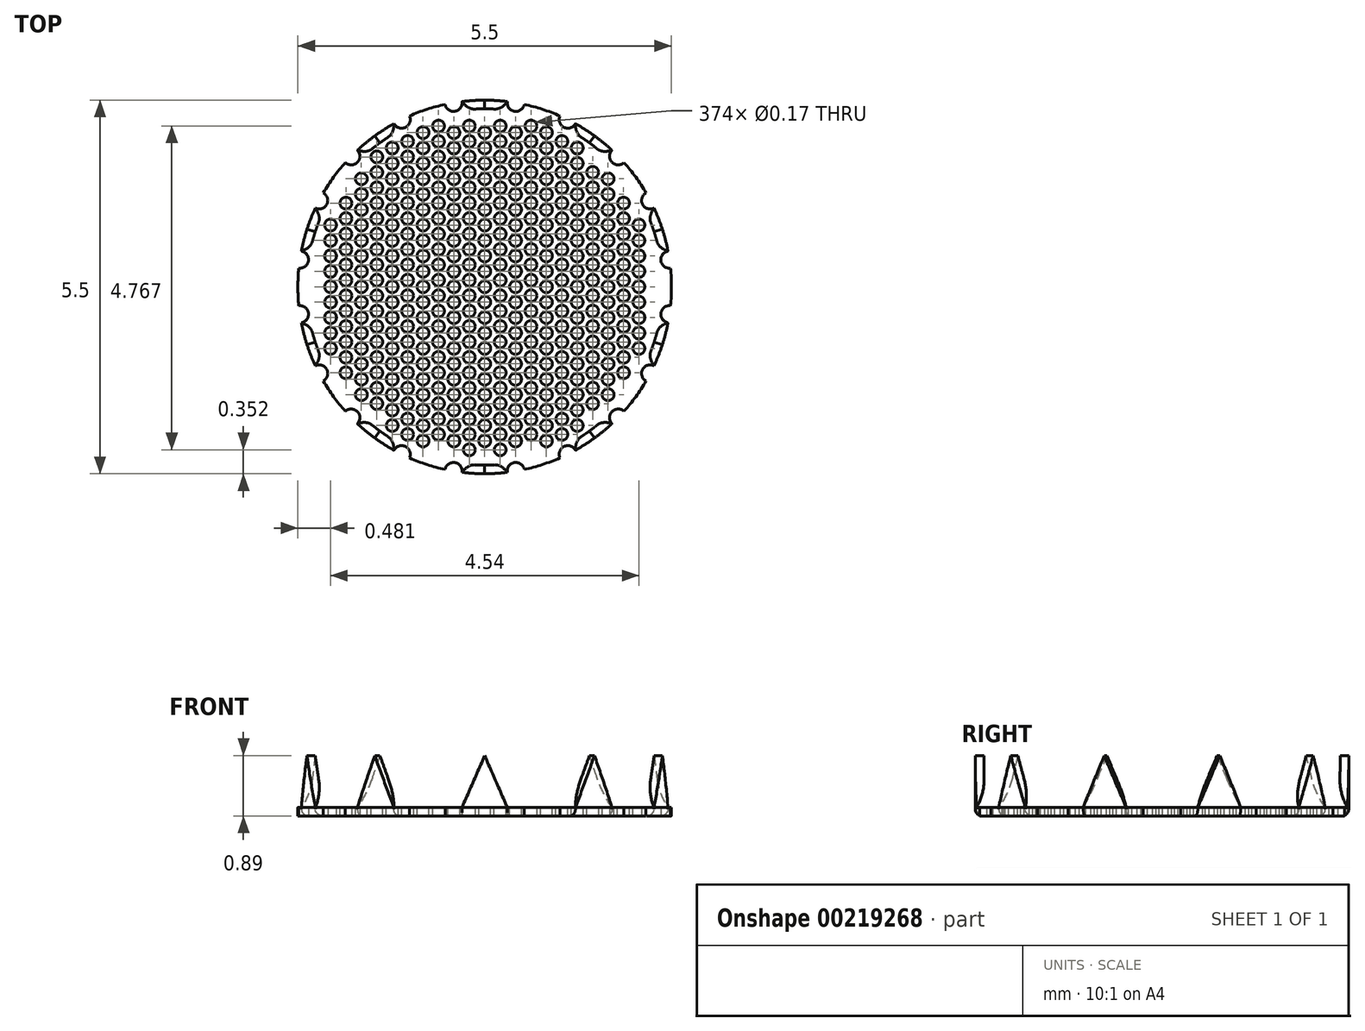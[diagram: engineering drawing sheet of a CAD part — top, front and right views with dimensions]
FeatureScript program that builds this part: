
annotation { "Feature Type Name" : "Feature", "Feature Type Description" : "" }
export const myFeature = defineFeature(function(context is Context, id is Id, definition is map)
    precondition{}
    {
        {
            var Q0;
            Q0=qCreatedBy(makeId("Top.planeOp"),FACE);
            var sketch = newSketch(context, id + "F0", { "sketchPlane" : qUnion([Q0])});
            skCircle(sketch, "E0", {"center": v(0, 0) * mm, "radius": 2.5 * mm});
            skArc(sketch, "E1", {"start": v(0.33, 2.73) * mm, "mid": v(0, 2.75) * mm, "end": v(-0.33, 2.73) * mm});
            skPoint(sketch, "E2", {"position": v(0, 2.75) * mm});
            skLineSegment(sketch, "E3", {"start": v(-3.94, 3.51) * mm, "end": v(3.7, 3.51) * mm, "construction": true});
            skLineSegment(sketch, "E4", {"start": v(0, 3.51) * mm, "end": v(-0.33, 2.73) * mm});
            skLineSegment(sketch, "E5", {"start": v(0, 3.51) * mm, "end": v(0.33, 2.73) * mm});
            skLineSegment(sketch, "E6.1.0", {"start": v(-2.06, 2.84) * mm, "end": v(-1.87, 2.01) * mm});
            skLineSegment(sketch, "E6.1.1", {"start": v(-2.06, 2.84) * mm, "end": v(-1.34, 2.4) * mm});
            skLineSegment(sketch, "E6.2.0", {"start": v(-3.34, 1.09) * mm, "end": v(-2.7, 0.53) * mm});
            skLineSegment(sketch, "E6.2.1", {"start": v(-3.34, 1.09) * mm, "end": v(-2.5, 1.16) * mm});
            skLineSegment(sketch, "E6.3.0", {"start": v(-3.34, -1.09) * mm, "end": v(-2.5, -1.16) * mm});
            skLineSegment(sketch, "E6.3.1", {"start": v(-3.34, -1.09) * mm, "end": v(-2.7, -0.53) * mm});
            skLineSegment(sketch, "E6.4.0", {"start": v(-2.06, -2.84) * mm, "end": v(-1.34, -2.4) * mm});
            skLineSegment(sketch, "E6.4.1", {"start": v(-2.06, -2.84) * mm, "end": v(-1.87, -2.01) * mm});
            skLineSegment(sketch, "E6.5.0", {"start": v(0, -3.51) * mm, "end": v(0.33, -2.73) * mm});
            skLineSegment(sketch, "E6.5.1", {"start": v(0, -3.51) * mm, "end": v(-0.33, -2.73) * mm});
            skLineSegment(sketch, "E6.6.0", {"start": v(2.06, -2.84) * mm, "end": v(1.87, -2.01) * mm});
            skLineSegment(sketch, "E6.6.1", {"start": v(2.06, -2.84) * mm, "end": v(1.34, -2.4) * mm});
            skLineSegment(sketch, "E6.7.0", {"start": v(3.34, -1.09) * mm, "end": v(2.7, -0.53) * mm});
            skLineSegment(sketch, "E6.7.1", {"start": v(3.34, -1.09) * mm, "end": v(2.5, -1.16) * mm});
            skLineSegment(sketch, "E6.8.0", {"start": v(3.34, 1.09) * mm, "end": v(2.5, 1.16) * mm});
            skLineSegment(sketch, "E6.8.1", {"start": v(3.34, 1.09) * mm, "end": v(2.7, 0.53) * mm});
            skLineSegment(sketch, "E6.9.0", {"start": v(2.06, 2.84) * mm, "end": v(1.34, 2.4) * mm});
            skLineSegment(sketch, "E6.9.1", {"start": v(2.06, 2.84) * mm, "end": v(1.87, 2.01) * mm});
            skCircle(sketch, "E7", {"center": v(0, 0) * mm, "radius": 2.62 * mm});
            skPoint(sketch, "E8", {"position": v(0.46, 2.71) * mm});
            skArc(sketch, "E9", {"start": v(0.33, 2.73) * mm, "mid": v(0.44, 2.59) * mm, "end": v(0.58, 2.69) * mm});
            skArc(sketch, "E10.1.0", {"start": v(-1.34, 2.4) * mm, "mid": v(-1.17, 2.35) * mm, "end": v(-1.1, 2.52) * mm});
            skArc(sketch, "E10.2.0", {"start": v(-2.5, 1.16) * mm, "mid": v(-2.32, 1.21) * mm, "end": v(-2.38, 1.38) * mm});
            skArc(sketch, "E10.3.0", {"start": v(-2.7, -0.53) * mm, "mid": v(-2.6, -0.38) * mm, "end": v(-2.74, -0.28) * mm});
            skArc(sketch, "E10.4.0", {"start": v(-1.87, -2.01) * mm, "mid": v(-1.87, -1.84) * mm, "end": v(-2.05, -1.83) * mm});
            skArc(sketch, "E10.5.0", {"start": v(-0.33, -2.73) * mm, "mid": v(-0.44, -2.59) * mm, "end": v(-0.58, -2.69) * mm});
            skArc(sketch, "E10.6.0", {"start": v(1.34, -2.4) * mm, "mid": v(1.17, -2.35) * mm, "end": v(1.1, -2.52) * mm});
            skArc(sketch, "E10.7.0", {"start": v(2.5, -1.16) * mm, "mid": v(2.32, -1.21) * mm, "end": v(2.38, -1.38) * mm});
            skArc(sketch, "E10.8.0", {"start": v(2.7, 0.53) * mm, "mid": v(2.6, 0.38) * mm, "end": v(2.74, 0.28) * mm});
            skArc(sketch, "E10.9.0", {"start": v(1.87, 2.01) * mm, "mid": v(1.87, 1.84) * mm, "end": v(2.05, 1.83) * mm});
            skArc(sketch, "E11", {"start": v(-0.58, 2.69) * mm, "mid": v(-0.44, 2.59) * mm, "end": v(-0.33, 2.73) * mm});
            skArc(sketch, "E12.trimOffspring", {"start": v(-0.58, 2.69) * mm, "mid": v(-0.85, 2.62) * mm, "end": v(-1.1, 2.52) * mm});
            skArc(sketch, "E13.1.0", {"start": v(-2.05, 1.83) * mm, "mid": v(-1.87, 1.84) * mm, "end": v(-1.87, 2.01) * mm});
            skArc(sketch, "E13.2.0", {"start": v(-2.74, 0.28) * mm, "mid": v(-2.6, 0.38) * mm, "end": v(-2.7, 0.53) * mm});
            skArc(sketch, "E13.3.0", {"start": v(-2.38, -1.38) * mm, "mid": v(-2.32, -1.21) * mm, "end": v(-2.5, -1.16) * mm});
            skArc(sketch, "E13.4.0", {"start": v(-1.1, -2.52) * mm, "mid": v(-1.17, -2.35) * mm, "end": v(-1.34, -2.4) * mm});
            skArc(sketch, "E13.5.0", {"start": v(0.58, -2.69) * mm, "mid": v(0.44, -2.59) * mm, "end": v(0.33, -2.73) * mm});
            skArc(sketch, "E13.6.0", {"start": v(2.05, -1.83) * mm, "mid": v(1.87, -1.84) * mm, "end": v(1.87, -2.01) * mm});
            skArc(sketch, "E13.7.0", {"start": v(2.74, -0.28) * mm, "mid": v(2.6, -0.38) * mm, "end": v(2.7, -0.53) * mm});
            skArc(sketch, "E13.8.0", {"start": v(2.38, 1.38) * mm, "mid": v(2.32, 1.21) * mm, "end": v(2.5, 1.16) * mm});
            skArc(sketch, "E13.9.0", {"start": v(1.1, 2.52) * mm, "mid": v(1.17, 2.35) * mm, "end": v(1.34, 2.4) * mm});
            skArc(sketch, "E14.trimOffspring", {"start": v(1.1, 2.52) * mm, "mid": v(0.85, 2.62) * mm, "end": v(0.58, 2.69) * mm});
            skArc(sketch, "E15.trimOffspring", {"start": v(1.87, 2.01) * mm, "mid": v(1.62, 2.22) * mm, "end": v(1.34, 2.4) * mm});
            skArc(sketch, "E16.trimOffspring", {"start": v(2.38, 1.38) * mm, "mid": v(2.22, 1.62) * mm, "end": v(2.05, 1.83) * mm});
            skArc(sketch, "E17.trimOffspring", {"start": v(2.7, 0.53) * mm, "mid": v(2.62, 0.85) * mm, "end": v(2.5, 1.16) * mm});
            skArc(sketch, "E18.trimOffspring", {"start": v(2.74, -0.28) * mm, "mid": v(2.75, 0) * mm, "end": v(2.74, 0.28) * mm});
            skArc(sketch, "E19.trimOffspring", {"start": v(2.5, -1.16) * mm, "mid": v(2.62, -0.85) * mm, "end": v(2.7, -0.53) * mm});
            skArc(sketch, "E20.trimOffspring", {"start": v(2.05, -1.83) * mm, "mid": v(2.22, -1.62) * mm, "end": v(2.38, -1.38) * mm});
            skArc(sketch, "E21.trimOffspring", {"start": v(1.34, -2.4) * mm, "mid": v(1.62, -2.22) * mm, "end": v(1.87, -2.01) * mm});
            skArc(sketch, "E22.trimOffspring", {"start": v(-2.38, -1.38) * mm, "mid": v(-2.22, -1.62) * mm, "end": v(-2.05, -1.83) * mm});
            skArc(sketch, "E23.trimOffspring", {"start": v(-1.87, -2.01) * mm, "mid": v(-1.62, -2.22) * mm, "end": v(-1.34, -2.4) * mm});
            skArc(sketch, "E24.trimOffspring", {"start": v(-1.1, -2.52) * mm, "mid": v(-0.85, -2.62) * mm, "end": v(-0.58, -2.69) * mm});
            skArc(sketch, "E25.trimOffspring", {"start": v(-0.33, -2.73) * mm, "mid": v(0, -2.75) * mm, "end": v(0.33, -2.73) * mm});
            skArc(sketch, "E26.trimOffspring", {"start": v(0.58, -2.69) * mm, "mid": v(0.85, -2.62) * mm, "end": v(1.1, -2.52) * mm});
            skArc(sketch, "E27.trimOffspring", {"start": v(-2.7, -0.53) * mm, "mid": v(-2.62, -0.85) * mm, "end": v(-2.5, -1.16) * mm});
            skArc(sketch, "E28.trimOffspring", {"start": v(-2.74, 0.28) * mm, "mid": v(-2.75, 0) * mm, "end": v(-2.74, -0.28) * mm});
            skArc(sketch, "E29.trimOffspring", {"start": v(-2.5, 1.16) * mm, "mid": v(-2.62, 0.85) * mm, "end": v(-2.7, 0.53) * mm});
            skArc(sketch, "E30.trimOffspring", {"start": v(-2.05, 1.83) * mm, "mid": v(-2.22, 1.62) * mm, "end": v(-2.38, 1.38) * mm});
            skArc(sketch, "E31.trimOffspring", {"start": v(-1.34, 2.4) * mm, "mid": v(-1.62, 2.22) * mm, "end": v(-1.87, 2.01) * mm});
            skSolve(sketch);
        }
        {
            var Q0;
            Q0=qSketchRegion(id+"F0",true);
            var Q1;
            Q1=makeQuery(id+"F0.imprint","IMPRINT",FACE,{"disambiguationData":[TD([[makeQuery(id+"F0.imprint","IMPRINT",EDGE,{"derivedFrom":sQuery(id+"F0.wireOp",EDGE,"E0")}),1.0]])]});
            extrude(context, id + "F1", {"entities" : qUnion([Q0, Q1]), "depth" : 0.13 * mm});
        }
        {
            var Q0;
            Q0=makeQuery(id+"F1.opExtrude","CAP_FACE",FACE,{"disambiguationData":[OSD([sQuery(id+"F0.wireOp",EDGE,"E1"),sQuery(id+"F0.wireOp",EDGE,"E4"),sQuery(id+"F0.wireOp",EDGE,"E5"),sQuery(id+"F0.wireOp",EDGE,"E6.1.0"),sQuery(id+"F0.wireOp",EDGE,"E6.1.1"),sQuery(id+"F0.wireOp",EDGE,"E6.2.0"),sQuery(id+"F0.wireOp",EDGE,"E6.2.1"),sQuery(id+"F0.wireOp",EDGE,"E6.3.0"),sQuery(id+"F0.wireOp",EDGE,"E6.3.1"),sQuery(id+"F0.wireOp",EDGE,"E6.4.0"),sQuery(id+"F0.wireOp",EDGE,"E6.4.1"),sQuery(id+"F0.wireOp",EDGE,"E6.5.0"),sQuery(id+"F0.wireOp",EDGE,"E6.5.1"),sQuery(id+"F0.wireOp",EDGE,"E6.6.0"),sQuery(id+"F0.wireOp",EDGE,"E6.6.1"),sQuery(id+"F0.wireOp",EDGE,"E6.7.0"),sQuery(id+"F0.wireOp",EDGE,"E6.7.1"),sQuery(id+"F0.wireOp",EDGE,"E6.8.0"),sQuery(id+"F0.wireOp",EDGE,"E6.8.1"),sQuery(id+"F0.wireOp",EDGE,"E6.9.0"),sQuery(id+"F0.wireOp",EDGE,"E6.9.1")])],"isStart":false});
            cPlane(context, id + "F2", {"entities" : qUnion([Q0]), "cplaneType" : CPlaneType.OFFSET, "offset" : 0 * mm, "width" : 150 * mm, "height" : 150 * mm});
        }
        {
            var Q0;
            Q0=qCreatedBy(id+"F2.planeOp",FACE);
            var sketch = newSketch(context, id + "F3", { "sketchPlane" : qUnion([Q0])});
            skCircle(sketch, "E32.2.1.8", {"center": v(-2.04, 1.23) * mm, "radius": 0.09 * mm});
            skCircle(sketch, "E32.2.1.9", {"center": v(-2.04, 1) * mm, "radius": 0.09 * mm});
            skCircle(sketch, "E32.0.1.10", {"center": v(-2.27, 0.91) * mm, "radius": 0.09 * mm});
            skCircle(sketch, "E32.2.1.10", {"center": v(-2.04, 0.78) * mm, "radius": 0.09 * mm});
            skCircle(sketch, "E32.2.2.5", {"center": v(-1.59, 1.91) * mm, "radius": 0.09 * mm});
            skCircle(sketch, "E32.2.2.6", {"center": v(-1.59, 1.69) * mm, "radius": 0.09 * mm});
            skCircle(sketch, "E32.0.2.7", {"center": v(-1.82, 1.6) * mm, "radius": 0.09 * mm});
            skCircle(sketch, "E32.2.2.7", {"center": v(-1.59, 1.46) * mm, "radius": 0.09 * mm});
            skCircle(sketch, "E32.0.2.8", {"center": v(-1.82, 1.36) * mm, "radius": 0.09 * mm});
            skCircle(sketch, "E32.2.2.8", {"center": v(-1.59, 1.23) * mm, "radius": 0.09 * mm});
            skCircle(sketch, "E32.0.2.9", {"center": v(-1.82, 1.14) * mm, "radius": 0.09 * mm});
            skCircle(sketch, "E32.2.2.9", {"center": v(-1.59, 1) * mm, "radius": 0.09 * mm});
            skCircle(sketch, "E32.0.2.10", {"center": v(-1.82, 0.91) * mm, "radius": 0.09 * mm});
            skCircle(sketch, "E32.2.2.10", {"center": v(-1.59, 0.78) * mm, "radius": 0.09 * mm});
            skCircle(sketch, "E32.2.3.4", {"center": v(-1.13, 2.14) * mm, "radius": 0.09 * mm});
            skCircle(sketch, "E32.0.3.5", {"center": v(-1.36, 2.05) * mm, "radius": 0.09 * mm});
            skCircle(sketch, "E32.2.3.5", {"center": v(-1.13, 1.91) * mm, "radius": 0.09 * mm});
            skCircle(sketch, "E32.0.3.6", {"center": v(-1.36, 1.82) * mm, "radius": 0.09 * mm});
            skCircle(sketch, "E32.2.3.6", {"center": v(-1.13, 1.69) * mm, "radius": 0.09 * mm});
            skCircle(sketch, "E32.0.3.7", {"center": v(-1.36, 1.6) * mm, "radius": 0.09 * mm});
            skCircle(sketch, "E32.2.3.7", {"center": v(-1.13, 1.46) * mm, "radius": 0.09 * mm});
            skCircle(sketch, "E32.0.3.8", {"center": v(-1.36, 1.36) * mm, "radius": 0.09 * mm});
            skCircle(sketch, "E32.2.3.8", {"center": v(-1.13, 1.23) * mm, "radius": 0.09 * mm});
            skCircle(sketch, "E32.0.3.9", {"center": v(-1.36, 1.14) * mm, "radius": 0.09 * mm});
            skCircle(sketch, "E32.2.3.9", {"center": v(-1.13, 1) * mm, "radius": 0.09 * mm});
            skCircle(sketch, "E32.0.3.10", {"center": v(-1.36, 0.91) * mm, "radius": 0.09 * mm});
            skCircle(sketch, "E32.2.3.10", {"center": v(-1.13, 0.78) * mm, "radius": 0.09 * mm});
            skCircle(sketch, "E32.2.4.3", {"center": v(-0.68, 2.37) * mm, "radius": 0.09 * mm});
            skCircle(sketch, "E32.0.4.4", {"center": v(-0.9, 2.27) * mm, "radius": 0.09 * mm});
            skCircle(sketch, "E32.2.4.4", {"center": v(-0.68, 2.14) * mm, "radius": 0.09 * mm});
            skCircle(sketch, "E32.0.4.5", {"center": v(-0.9, 2.05) * mm, "radius": 0.09 * mm});
            skCircle(sketch, "E32.2.4.5", {"center": v(-0.68, 1.91) * mm, "radius": 0.09 * mm});
            skCircle(sketch, "E32.0.4.6", {"center": v(-0.9, 1.82) * mm, "radius": 0.09 * mm});
            skCircle(sketch, "E32.2.4.6", {"center": v(-0.68, 1.69) * mm, "radius": 0.09 * mm});
            skCircle(sketch, "E32.0.4.7", {"center": v(-0.9, 1.6) * mm, "radius": 0.09 * mm});
            skCircle(sketch, "E32.2.4.7", {"center": v(-0.68, 1.46) * mm, "radius": 0.09 * mm});
            skCircle(sketch, "E32.0.4.8", {"center": v(-0.9, 1.36) * mm, "radius": 0.09 * mm});
            skCircle(sketch, "E32.2.4.8", {"center": v(-0.68, 1.23) * mm, "radius": 0.09 * mm});
            skCircle(sketch, "E32.0.4.9", {"center": v(-0.9, 1.14) * mm, "radius": 0.09 * mm});
            skCircle(sketch, "E32.2.4.9", {"center": v(-0.68, 1) * mm, "radius": 0.09 * mm});
            skCircle(sketch, "E32.0.4.10", {"center": v(-0.9, 0.91) * mm, "radius": 0.09 * mm});
            skCircle(sketch, "E32.2.4.10", {"center": v(-0.68, 0.78) * mm, "radius": 0.09 * mm});
            skCircle(sketch, "E32.2.5.3", {"center": v(-0.23, 2.37) * mm, "radius": 0.09 * mm});
            skCircle(sketch, "E32.0.5.4", {"center": v(-0.45, 2.27) * mm, "radius": 0.09 * mm});
            skCircle(sketch, "E32.2.5.4", {"center": v(-0.23, 2.14) * mm, "radius": 0.09 * mm});
            skCircle(sketch, "E32.0.5.5", {"center": v(-0.45, 2.05) * mm, "radius": 0.09 * mm});
            skCircle(sketch, "E32.2.5.5", {"center": v(-0.23, 1.91) * mm, "radius": 0.09 * mm});
            skCircle(sketch, "E32.0.5.6", {"center": v(-0.45, 1.82) * mm, "radius": 0.09 * mm});
            skCircle(sketch, "E32.2.5.6", {"center": v(-0.23, 1.69) * mm, "radius": 0.09 * mm});
            skCircle(sketch, "E32.0.5.7", {"center": v(-0.45, 1.6) * mm, "radius": 0.09 * mm});
            skCircle(sketch, "E32.2.5.7", {"center": v(-0.23, 1.46) * mm, "radius": 0.09 * mm});
            skCircle(sketch, "E32.0.5.8", {"center": v(-0.45, 1.36) * mm, "radius": 0.09 * mm});
            skCircle(sketch, "E32.2.5.8", {"center": v(-0.23, 1.23) * mm, "radius": 0.09 * mm});
            skCircle(sketch, "E32.0.5.9", {"center": v(-0.45, 1.14) * mm, "radius": 0.09 * mm});
            skCircle(sketch, "E32.2.5.9", {"center": v(-0.23, 1) * mm, "radius": 0.09 * mm});
            skCircle(sketch, "E32.0.5.10", {"center": v(-0.45, 0.91) * mm, "radius": 0.09 * mm});
            skCircle(sketch, "E32.2.5.10", {"center": v(-0.23, 0.78) * mm, "radius": 0.09 * mm});
            skCircle(sketch, "E32.2.6.3", {"center": v(0.23, 2.37) * mm, "radius": 0.09 * mm});
            skCircle(sketch, "E32.0.6.4", {"center": v(0, 2.27) * mm, "radius": 0.09 * mm});
            skCircle(sketch, "E32.2.6.4", {"center": v(0.23, 2.14) * mm, "radius": 0.09 * mm});
            skCircle(sketch, "E32.0.6.5", {"center": v(0, 2.05) * mm, "radius": 0.09 * mm});
            skCircle(sketch, "E32.2.6.5", {"center": v(0.23, 1.91) * mm, "radius": 0.09 * mm});
            skCircle(sketch, "E32.0.6.6", {"center": v(0, 1.82) * mm, "radius": 0.09 * mm});
            skCircle(sketch, "E32.2.6.6", {"center": v(0.23, 1.69) * mm, "radius": 0.09 * mm});
            skCircle(sketch, "E32.0.6.7", {"center": v(0, 1.6) * mm, "radius": 0.09 * mm});
            skCircle(sketch, "E32.2.6.7", {"center": v(0.23, 1.46) * mm, "radius": 0.09 * mm});
            skCircle(sketch, "E32.0.6.8", {"center": v(0, 1.36) * mm, "radius": 0.09 * mm});
            skCircle(sketch, "E32.2.6.8", {"center": v(0.23, 1.23) * mm, "radius": 0.09 * mm});
            skCircle(sketch, "E32.0.6.9", {"center": v(0, 1.14) * mm, "radius": 0.09 * mm});
            skCircle(sketch, "E32.2.6.9", {"center": v(0.23, 1) * mm, "radius": 0.09 * mm});
            skCircle(sketch, "E32.0.6.10", {"center": v(0, 0.91) * mm, "radius": 0.09 * mm});
            skCircle(sketch, "E32.2.6.10", {"center": v(0.23, 0.78) * mm, "radius": 0.09 * mm});
            skCircle(sketch, "E32.2.7.3", {"center": v(0.68, 2.37) * mm, "radius": 0.09 * mm});
            skCircle(sketch, "E32.0.7.4", {"center": v(0.45, 2.27) * mm, "radius": 0.09 * mm});
            skCircle(sketch, "E32.2.7.4", {"center": v(0.68, 2.14) * mm, "radius": 0.09 * mm});
            skCircle(sketch, "E32.0.7.5", {"center": v(0.45, 2.05) * mm, "radius": 0.09 * mm});
            skCircle(sketch, "E32.2.7.5", {"center": v(0.68, 1.91) * mm, "radius": 0.09 * mm});
            skCircle(sketch, "E32.0.7.6", {"center": v(0.45, 1.82) * mm, "radius": 0.09 * mm});
            skCircle(sketch, "E32.2.7.6", {"center": v(0.68, 1.69) * mm, "radius": 0.09 * mm});
            skCircle(sketch, "E32.0.7.7", {"center": v(0.45, 1.6) * mm, "radius": 0.09 * mm});
            skCircle(sketch, "E32.2.7.7", {"center": v(0.68, 1.46) * mm, "radius": 0.09 * mm});
            skCircle(sketch, "E32.0.7.8", {"center": v(0.45, 1.36) * mm, "radius": 0.09 * mm});
            skCircle(sketch, "E32.2.7.8", {"center": v(0.68, 1.23) * mm, "radius": 0.09 * mm});
            skCircle(sketch, "E32.0.7.9", {"center": v(0.45, 1.14) * mm, "radius": 0.09 * mm});
            skCircle(sketch, "E32.2.7.9", {"center": v(0.68, 1) * mm, "radius": 0.09 * mm});
            skCircle(sketch, "E32.0.7.10", {"center": v(0.45, 0.91) * mm, "radius": 0.09 * mm});
            skCircle(sketch, "E32.2.7.10", {"center": v(0.68, 0.78) * mm, "radius": 0.09 * mm});
            skCircle(sketch, "E32.0.8.4", {"center": v(0.9, 2.27) * mm, "radius": 0.09 * mm});
            skCircle(sketch, "E32.2.8.4", {"center": v(1.14, 2.14) * mm, "radius": 0.09 * mm});
            skCircle(sketch, "E32.0.8.5", {"center": v(0.9, 2.05) * mm, "radius": 0.09 * mm});
            skCircle(sketch, "E32.2.8.5", {"center": v(1.14, 1.91) * mm, "radius": 0.09 * mm});
            skCircle(sketch, "E32.0.8.6", {"center": v(0.9, 1.82) * mm, "radius": 0.09 * mm});
            skCircle(sketch, "E32.2.8.6", {"center": v(1.14, 1.69) * mm, "radius": 0.09 * mm});
            skCircle(sketch, "E32.0.8.7", {"center": v(0.9, 1.6) * mm, "radius": 0.09 * mm});
            skCircle(sketch, "E32.2.8.7", {"center": v(1.14, 1.46) * mm, "radius": 0.09 * mm});
            skCircle(sketch, "E32.0.8.8", {"center": v(0.9, 1.36) * mm, "radius": 0.09 * mm});
            skCircle(sketch, "E32.2.8.8", {"center": v(1.14, 1.23) * mm, "radius": 0.09 * mm});
            skCircle(sketch, "E32.0.8.9", {"center": v(0.9, 1.14) * mm, "radius": 0.09 * mm});
            skCircle(sketch, "E32.2.8.9", {"center": v(1.14, 1) * mm, "radius": 0.09 * mm});
            skCircle(sketch, "E32.0.8.10", {"center": v(0.9, 0.91) * mm, "radius": 0.09 * mm});
            skCircle(sketch, "E32.2.8.10", {"center": v(1.14, 0.78) * mm, "radius": 0.09 * mm});
            skCircle(sketch, "E32.0.9.5", {"center": v(1.36, 2.05) * mm, "radius": 0.09 * mm});
            skCircle(sketch, "E32.0.9.6", {"center": v(1.36, 1.82) * mm, "radius": 0.09 * mm});
            skCircle(sketch, "E32.2.9.6", {"center": v(1.6, 1.69) * mm, "radius": 0.09 * mm});
            skCircle(sketch, "E32.0.9.7", {"center": v(1.36, 1.6) * mm, "radius": 0.09 * mm});
            skCircle(sketch, "E32.2.9.7", {"center": v(1.6, 1.46) * mm, "radius": 0.09 * mm});
            skCircle(sketch, "E32.0.9.8", {"center": v(1.36, 1.36) * mm, "radius": 0.09 * mm});
            skCircle(sketch, "E32.2.9.8", {"center": v(1.6, 1.23) * mm, "radius": 0.09 * mm});
            skCircle(sketch, "E32.0.9.9", {"center": v(1.36, 1.14) * mm, "radius": 0.09 * mm});
            skCircle(sketch, "E32.2.9.9", {"center": v(1.6, 1) * mm, "radius": 0.09 * mm});
            skCircle(sketch, "E32.0.9.10", {"center": v(1.36, 0.91) * mm, "radius": 0.09 * mm});
            skCircle(sketch, "E32.2.9.10", {"center": v(1.6, 0.78) * mm, "radius": 0.09 * mm});
            skCircle(sketch, "E32.0.10.7", {"center": v(1.82, 1.6) * mm, "radius": 0.09 * mm});
            skCircle(sketch, "E32.0.10.8", {"center": v(1.82, 1.36) * mm, "radius": 0.09 * mm});
            skCircle(sketch, "E32.2.10.8", {"center": v(2.04, 1.23) * mm, "radius": 0.09 * mm});
            skCircle(sketch, "E32.0.10.9", {"center": v(1.82, 1.14) * mm, "radius": 0.09 * mm});
            skCircle(sketch, "E32.2.10.9", {"center": v(2.04, 1) * mm, "radius": 0.09 * mm});
            skCircle(sketch, "E32.0.10.10", {"center": v(1.82, 0.91) * mm, "radius": 0.09 * mm});
            skCircle(sketch, "E32.2.10.10", {"center": v(2.04, 0.78) * mm, "radius": 0.09 * mm});
            skCircle(sketch, "E33.0.1.11", {"center": v(-2.27, 0.68) * mm, "radius": 0.09 * mm});
            skCircle(sketch, "E33.2.1.11", {"center": v(-2.04, 0.55) * mm, "radius": 0.09 * mm});
            skCircle(sketch, "E33.0.1.12", {"center": v(-2.27, 0.46) * mm, "radius": 0.09 * mm});
            skCircle(sketch, "E33.2.1.12", {"center": v(-2.04, 0.33) * mm, "radius": 0.09 * mm});
            skCircle(sketch, "E33.0.1.13", {"center": v(-2.27, 0.23) * mm, "radius": 0.09 * mm});
            skCircle(sketch, "E33.2.1.13", {"center": v(-2.04, 0.1) * mm, "radius": 0.09 * mm});
            skCircle(sketch, "E33.0.1.14", {"center": v(-2.27, 0) * mm, "radius": 0.09 * mm});
            skCircle(sketch, "E33.2.1.14", {"center": v(-2.04, -0.13) * mm, "radius": 0.09 * mm});
            skCircle(sketch, "E33.0.1.15", {"center": v(-2.27, -0.22) * mm, "radius": 0.09 * mm});
            skCircle(sketch, "E33.2.1.15", {"center": v(-2.04, -0.36) * mm, "radius": 0.09 * mm});
            skCircle(sketch, "E33.0.1.16", {"center": v(-2.27, -0.45) * mm, "radius": 0.09 * mm});
            skCircle(sketch, "E33.2.1.16", {"center": v(-2.04, -0.58) * mm, "radius": 0.09 * mm});
            skCircle(sketch, "E33.0.1.17", {"center": v(-2.27, -0.68) * mm, "radius": 0.09 * mm});
            skCircle(sketch, "E33.2.1.17", {"center": v(-2.04, -0.8) * mm, "radius": 0.09 * mm});
            skCircle(sketch, "E33.0.1.18", {"center": v(-2.27, -0.9) * mm, "radius": 0.09 * mm});
            skCircle(sketch, "E33.2.1.18", {"center": v(-2.04, -1.04) * mm, "radius": 0.09 * mm});
            skCircle(sketch, "E33.2.1.19", {"center": v(-2.04, -1.26) * mm, "radius": 0.09 * mm});
            skCircle(sketch, "E33.0.2.11", {"center": v(-1.82, 0.68) * mm, "radius": 0.09 * mm});
            skCircle(sketch, "E33.2.2.11", {"center": v(-1.59, 0.55) * mm, "radius": 0.09 * mm});
            skCircle(sketch, "E33.0.2.12", {"center": v(-1.82, 0.46) * mm, "radius": 0.09 * mm});
            skCircle(sketch, "E33.2.2.12", {"center": v(-1.59, 0.33) * mm, "radius": 0.09 * mm});
            skCircle(sketch, "E33.0.2.13", {"center": v(-1.82, 0.23) * mm, "radius": 0.09 * mm});
            skCircle(sketch, "E33.2.2.13", {"center": v(-1.59, 0.1) * mm, "radius": 0.09 * mm});
            skCircle(sketch, "E33.0.2.14", {"center": v(-1.82, 0) * mm, "radius": 0.09 * mm});
            skCircle(sketch, "E33.2.2.14", {"center": v(-1.59, -0.13) * mm, "radius": 0.09 * mm});
            skCircle(sketch, "E33.0.2.15", {"center": v(-1.82, -0.22) * mm, "radius": 0.09 * mm});
            skCircle(sketch, "E33.2.2.15", {"center": v(-1.59, -0.36) * mm, "radius": 0.09 * mm});
            skCircle(sketch, "E33.0.2.16", {"center": v(-1.82, -0.45) * mm, "radius": 0.09 * mm});
            skCircle(sketch, "E33.2.2.16", {"center": v(-1.59, -0.58) * mm, "radius": 0.09 * mm});
            skCircle(sketch, "E33.0.2.17", {"center": v(-1.82, -0.68) * mm, "radius": 0.09 * mm});
            skCircle(sketch, "E33.2.2.17", {"center": v(-1.59, -0.8) * mm, "radius": 0.09 * mm});
            skCircle(sketch, "E33.0.2.18", {"center": v(-1.82, -0.9) * mm, "radius": 0.09 * mm});
            skCircle(sketch, "E33.2.2.18", {"center": v(-1.59, -1.04) * mm, "radius": 0.09 * mm});
            skCircle(sketch, "E33.0.2.19", {"center": v(-1.82, -1.13) * mm, "radius": 0.09 * mm});
            skCircle(sketch, "E33.2.2.19", {"center": v(-1.59, -1.26) * mm, "radius": 0.09 * mm});
            skCircle(sketch, "E33.0.2.20", {"center": v(-1.82, -1.36) * mm, "radius": 0.09 * mm});
            skCircle(sketch, "E33.2.2.20", {"center": v(-1.59, -1.5) * mm, "radius": 0.09 * mm});
            skCircle(sketch, "E33.0.2.21", {"center": v(-1.82, -1.59) * mm, "radius": 0.09 * mm});
            skCircle(sketch, "E33.2.2.21", {"center": v(-1.59, -1.72) * mm, "radius": 0.09 * mm});
            skCircle(sketch, "E33.0.3.11", {"center": v(-1.36, 0.68) * mm, "radius": 0.09 * mm});
            skCircle(sketch, "E33.2.3.11", {"center": v(-1.13, 0.55) * mm, "radius": 0.09 * mm});
            skCircle(sketch, "E33.0.3.12", {"center": v(-1.36, 0.46) * mm, "radius": 0.09 * mm});
            skCircle(sketch, "E33.2.3.12", {"center": v(-1.13, 0.33) * mm, "radius": 0.09 * mm});
            skCircle(sketch, "E33.0.3.13", {"center": v(-1.36, 0.23) * mm, "radius": 0.09 * mm});
            skCircle(sketch, "E33.2.3.13", {"center": v(-1.13, 0.1) * mm, "radius": 0.09 * mm});
            skCircle(sketch, "E33.0.3.14", {"center": v(-1.36, 0) * mm, "radius": 0.09 * mm});
            skCircle(sketch, "E33.2.3.14", {"center": v(-1.13, -0.13) * mm, "radius": 0.09 * mm});
            skCircle(sketch, "E33.0.3.15", {"center": v(-1.36, -0.22) * mm, "radius": 0.09 * mm});
            skCircle(sketch, "E33.2.3.15", {"center": v(-1.13, -0.36) * mm, "radius": 0.09 * mm});
            skCircle(sketch, "E33.0.3.16", {"center": v(-1.36, -0.45) * mm, "radius": 0.09 * mm});
            skCircle(sketch, "E33.2.3.16", {"center": v(-1.13, -0.58) * mm, "radius": 0.09 * mm});
            skCircle(sketch, "E33.0.3.17", {"center": v(-1.36, -0.68) * mm, "radius": 0.09 * mm});
            skCircle(sketch, "E33.2.3.17", {"center": v(-1.13, -0.8) * mm, "radius": 0.09 * mm});
            skCircle(sketch, "E33.0.3.18", {"center": v(-1.36, -0.9) * mm, "radius": 0.09 * mm});
            skCircle(sketch, "E33.2.3.18", {"center": v(-1.13, -1.04) * mm, "radius": 0.09 * mm});
            skCircle(sketch, "E33.0.3.19", {"center": v(-1.36, -1.13) * mm, "radius": 0.09 * mm});
            skCircle(sketch, "E33.2.3.19", {"center": v(-1.13, -1.26) * mm, "radius": 0.09 * mm});
            skCircle(sketch, "E33.0.3.20", {"center": v(-1.36, -1.36) * mm, "radius": 0.09 * mm});
            skCircle(sketch, "E33.2.3.20", {"center": v(-1.13, -1.5) * mm, "radius": 0.09 * mm});
            skCircle(sketch, "E33.0.3.21", {"center": v(-1.36, -1.59) * mm, "radius": 0.09 * mm});
            skCircle(sketch, "E33.2.3.21", {"center": v(-1.13, -1.72) * mm, "radius": 0.09 * mm});
            skCircle(sketch, "E33.0.4.11", {"center": v(-0.9, 0.68) * mm, "radius": 0.09 * mm});
            skCircle(sketch, "E33.2.4.11", {"center": v(-0.68, 0.55) * mm, "radius": 0.09 * mm});
            skCircle(sketch, "E33.0.4.12", {"center": v(-0.9, 0.46) * mm, "radius": 0.09 * mm});
            skCircle(sketch, "E33.2.4.12", {"center": v(-0.68, 0.33) * mm, "radius": 0.09 * mm});
            skCircle(sketch, "E33.0.4.13", {"center": v(-0.9, 0.23) * mm, "radius": 0.09 * mm});
            skCircle(sketch, "E33.2.4.13", {"center": v(-0.68, 0.1) * mm, "radius": 0.09 * mm});
            skCircle(sketch, "E33.0.4.14", {"center": v(-0.9, 0) * mm, "radius": 0.09 * mm});
            skCircle(sketch, "E33.2.4.14", {"center": v(-0.68, -0.13) * mm, "radius": 0.09 * mm});
            skCircle(sketch, "E33.0.4.15", {"center": v(-0.9, -0.22) * mm, "radius": 0.09 * mm});
            skCircle(sketch, "E33.2.4.15", {"center": v(-0.68, -0.36) * mm, "radius": 0.09 * mm});
            skCircle(sketch, "E33.0.4.16", {"center": v(-0.9, -0.45) * mm, "radius": 0.09 * mm});
            skCircle(sketch, "E33.2.4.16", {"center": v(-0.68, -0.58) * mm, "radius": 0.09 * mm});
            skCircle(sketch, "E33.0.4.17", {"center": v(-0.9, -0.68) * mm, "radius": 0.09 * mm});
            skCircle(sketch, "E33.2.4.17", {"center": v(-0.68, -0.8) * mm, "radius": 0.09 * mm});
            skCircle(sketch, "E33.0.4.18", {"center": v(-0.9, -0.9) * mm, "radius": 0.09 * mm});
            skCircle(sketch, "E33.2.4.18", {"center": v(-0.68, -1.04) * mm, "radius": 0.09 * mm});
            skCircle(sketch, "E33.0.4.19", {"center": v(-0.9, -1.13) * mm, "radius": 0.09 * mm});
            skCircle(sketch, "E33.2.4.19", {"center": v(-0.68, -1.26) * mm, "radius": 0.09 * mm});
            skCircle(sketch, "E33.0.4.20", {"center": v(-0.9, -1.36) * mm, "radius": 0.09 * mm});
            skCircle(sketch, "E33.2.4.20", {"center": v(-0.68, -1.5) * mm, "radius": 0.09 * mm});
            skCircle(sketch, "E33.0.4.21", {"center": v(-0.9, -1.59) * mm, "radius": 0.09 * mm});
            skCircle(sketch, "E33.2.4.21", {"center": v(-0.68, -1.72) * mm, "radius": 0.09 * mm});
            skCircle(sketch, "E33.0.5.11", {"center": v(-0.45, 0.68) * mm, "radius": 0.09 * mm});
            skCircle(sketch, "E33.2.5.11", {"center": v(-0.23, 0.55) * mm, "radius": 0.09 * mm});
            skCircle(sketch, "E33.0.5.12", {"center": v(-0.45, 0.46) * mm, "radius": 0.09 * mm});
            skCircle(sketch, "E33.2.5.12", {"center": v(-0.23, 0.33) * mm, "radius": 0.09 * mm});
            skCircle(sketch, "E33.0.5.13", {"center": v(-0.45, 0.23) * mm, "radius": 0.09 * mm});
            skCircle(sketch, "E33.2.5.13", {"center": v(-0.23, 0.1) * mm, "radius": 0.09 * mm});
            skCircle(sketch, "E33.0.5.14", {"center": v(-0.45, 0) * mm, "radius": 0.09 * mm});
            skCircle(sketch, "E33.2.5.14", {"center": v(-0.23, -0.13) * mm, "radius": 0.09 * mm});
            skCircle(sketch, "E33.0.5.15", {"center": v(-0.45, -0.22) * mm, "radius": 0.09 * mm});
            skCircle(sketch, "E33.2.5.15", {"center": v(-0.23, -0.36) * mm, "radius": 0.09 * mm});
            skCircle(sketch, "E33.0.5.16", {"center": v(-0.45, -0.45) * mm, "radius": 0.09 * mm});
            skCircle(sketch, "E33.2.5.16", {"center": v(-0.23, -0.58) * mm, "radius": 0.09 * mm});
            skCircle(sketch, "E33.0.5.17", {"center": v(-0.45, -0.68) * mm, "radius": 0.09 * mm});
            skCircle(sketch, "E33.2.5.17", {"center": v(-0.23, -0.8) * mm, "radius": 0.09 * mm});
            skCircle(sketch, "E33.0.5.18", {"center": v(-0.45, -0.9) * mm, "radius": 0.09 * mm});
            skCircle(sketch, "E33.2.5.18", {"center": v(-0.23, -1.04) * mm, "radius": 0.09 * mm});
            skCircle(sketch, "E33.0.5.19", {"center": v(-0.45, -1.13) * mm, "radius": 0.09 * mm});
            skCircle(sketch, "E33.2.5.19", {"center": v(-0.23, -1.26) * mm, "radius": 0.09 * mm});
            skCircle(sketch, "E33.0.5.20", {"center": v(-0.45, -1.36) * mm, "radius": 0.09 * mm});
            skCircle(sketch, "E33.2.5.20", {"center": v(-0.23, -1.5) * mm, "radius": 0.09 * mm});
            skCircle(sketch, "E33.0.5.21", {"center": v(-0.45, -1.59) * mm, "radius": 0.09 * mm});
            skCircle(sketch, "E33.2.5.21", {"center": v(-0.23, -1.72) * mm, "radius": 0.09 * mm});
            skCircle(sketch, "E33.0.6.11", {"center": v(0, 0.68) * mm, "radius": 0.09 * mm});
            skCircle(sketch, "E33.2.6.11", {"center": v(0.23, 0.55) * mm, "radius": 0.09 * mm});
            skCircle(sketch, "E33.0.6.12", {"center": v(0, 0.46) * mm, "radius": 0.09 * mm});
            skCircle(sketch, "E33.2.6.12", {"center": v(0.23, 0.33) * mm, "radius": 0.09 * mm});
            skCircle(sketch, "E33.0.6.13", {"center": v(0, 0.23) * mm, "radius": 0.09 * mm});
            skCircle(sketch, "E33.2.6.13", {"center": v(0.23, 0.1) * mm, "radius": 0.09 * mm});
            skCircle(sketch, "E33.0.6.14", {"center": v(0, 0) * mm, "radius": 0.09 * mm});
            skCircle(sketch, "E33.2.6.14", {"center": v(0.23, -0.13) * mm, "radius": 0.09 * mm});
            skCircle(sketch, "E33.0.6.15", {"center": v(0, -0.22) * mm, "radius": 0.09 * mm});
            skCircle(sketch, "E33.2.6.15", {"center": v(0.23, -0.36) * mm, "radius": 0.09 * mm});
            skCircle(sketch, "E33.0.6.16", {"center": v(0, -0.45) * mm, "radius": 0.09 * mm});
            skCircle(sketch, "E33.2.6.16", {"center": v(0.23, -0.58) * mm, "radius": 0.09 * mm});
            skCircle(sketch, "E33.0.6.17", {"center": v(0, -0.68) * mm, "radius": 0.09 * mm});
            skCircle(sketch, "E33.2.6.17", {"center": v(0.23, -0.8) * mm, "radius": 0.09 * mm});
            skCircle(sketch, "E33.0.6.18", {"center": v(0, -0.9) * mm, "radius": 0.09 * mm});
            skCircle(sketch, "E33.2.6.18", {"center": v(0.23, -1.04) * mm, "radius": 0.09 * mm});
            skCircle(sketch, "E33.0.6.19", {"center": v(0, -1.13) * mm, "radius": 0.09 * mm});
            skCircle(sketch, "E33.2.6.19", {"center": v(0.23, -1.26) * mm, "radius": 0.09 * mm});
            skCircle(sketch, "E33.0.6.20", {"center": v(0, -1.36) * mm, "radius": 0.09 * mm});
            skCircle(sketch, "E33.2.6.20", {"center": v(0.23, -1.5) * mm, "radius": 0.09 * mm});
            skCircle(sketch, "E33.0.6.21", {"center": v(0, -1.59) * mm, "radius": 0.09 * mm});
            skCircle(sketch, "E33.2.6.21", {"center": v(0.23, -1.72) * mm, "radius": 0.09 * mm});
            skCircle(sketch, "E33.0.7.11", {"center": v(0.45, 0.68) * mm, "radius": 0.09 * mm});
            skCircle(sketch, "E33.2.7.11", {"center": v(0.68, 0.55) * mm, "radius": 0.09 * mm});
            skCircle(sketch, "E33.0.7.12", {"center": v(0.45, 0.46) * mm, "radius": 0.09 * mm});
            skCircle(sketch, "E33.2.7.12", {"center": v(0.68, 0.33) * mm, "radius": 0.09 * mm});
            skCircle(sketch, "E33.0.7.13", {"center": v(0.45, 0.23) * mm, "radius": 0.09 * mm});
            skCircle(sketch, "E33.2.7.13", {"center": v(0.68, 0.1) * mm, "radius": 0.09 * mm});
            skCircle(sketch, "E33.0.7.14", {"center": v(0.45, 0) * mm, "radius": 0.09 * mm});
            skCircle(sketch, "E33.2.7.14", {"center": v(0.68, -0.13) * mm, "radius": 0.09 * mm});
            skCircle(sketch, "E33.0.7.15", {"center": v(0.45, -0.22) * mm, "radius": 0.09 * mm});
            skCircle(sketch, "E33.2.7.15", {"center": v(0.68, -0.36) * mm, "radius": 0.09 * mm});
            skCircle(sketch, "E33.0.7.16", {"center": v(0.45, -0.45) * mm, "radius": 0.09 * mm});
            skCircle(sketch, "E33.2.7.16", {"center": v(0.68, -0.58) * mm, "radius": 0.09 * mm});
            skCircle(sketch, "E33.0.7.17", {"center": v(0.45, -0.68) * mm, "radius": 0.09 * mm});
            skCircle(sketch, "E33.2.7.17", {"center": v(0.68, -0.8) * mm, "radius": 0.09 * mm});
            skCircle(sketch, "E33.0.7.18", {"center": v(0.45, -0.9) * mm, "radius": 0.09 * mm});
            skCircle(sketch, "E33.2.7.18", {"center": v(0.68, -1.04) * mm, "radius": 0.09 * mm});
            skCircle(sketch, "E33.0.7.19", {"center": v(0.45, -1.13) * mm, "radius": 0.09 * mm});
            skCircle(sketch, "E33.2.7.19", {"center": v(0.68, -1.26) * mm, "radius": 0.09 * mm});
            skCircle(sketch, "E33.0.7.20", {"center": v(0.45, -1.36) * mm, "radius": 0.09 * mm});
            skCircle(sketch, "E33.2.7.20", {"center": v(0.68, -1.5) * mm, "radius": 0.09 * mm});
            skCircle(sketch, "E33.0.7.21", {"center": v(0.45, -1.59) * mm, "radius": 0.09 * mm});
            skCircle(sketch, "E33.2.7.21", {"center": v(0.68, -1.72) * mm, "radius": 0.09 * mm});
            skCircle(sketch, "E33.0.8.11", {"center": v(0.9, 0.68) * mm, "radius": 0.09 * mm});
            skCircle(sketch, "E33.2.8.11", {"center": v(1.14, 0.55) * mm, "radius": 0.09 * mm});
            skCircle(sketch, "E33.0.8.12", {"center": v(0.9, 0.46) * mm, "radius": 0.09 * mm});
            skCircle(sketch, "E33.2.8.12", {"center": v(1.14, 0.33) * mm, "radius": 0.09 * mm});
            skCircle(sketch, "E33.0.8.13", {"center": v(0.9, 0.23) * mm, "radius": 0.09 * mm});
            skCircle(sketch, "E33.2.8.13", {"center": v(1.14, 0.1) * mm, "radius": 0.09 * mm});
            skCircle(sketch, "E33.0.8.14", {"center": v(0.9, 0) * mm, "radius": 0.09 * mm});
            skCircle(sketch, "E33.2.8.14", {"center": v(1.14, -0.13) * mm, "radius": 0.09 * mm});
            skCircle(sketch, "E33.0.8.15", {"center": v(0.9, -0.22) * mm, "radius": 0.09 * mm});
            skCircle(sketch, "E33.2.8.15", {"center": v(1.14, -0.36) * mm, "radius": 0.09 * mm});
            skCircle(sketch, "E33.0.8.16", {"center": v(0.9, -0.45) * mm, "radius": 0.09 * mm});
            skCircle(sketch, "E33.2.8.16", {"center": v(1.14, -0.58) * mm, "radius": 0.09 * mm});
            skCircle(sketch, "E33.0.8.17", {"center": v(0.9, -0.68) * mm, "radius": 0.09 * mm});
            skCircle(sketch, "E33.2.8.17", {"center": v(1.14, -0.8) * mm, "radius": 0.09 * mm});
            skCircle(sketch, "E33.0.8.18", {"center": v(0.9, -0.9) * mm, "radius": 0.09 * mm});
            skCircle(sketch, "E33.2.8.18", {"center": v(1.14, -1.04) * mm, "radius": 0.09 * mm});
            skCircle(sketch, "E33.0.8.19", {"center": v(0.9, -1.13) * mm, "radius": 0.09 * mm});
            skCircle(sketch, "E33.2.8.19", {"center": v(1.14, -1.26) * mm, "radius": 0.09 * mm});
            skCircle(sketch, "E33.0.8.20", {"center": v(0.9, -1.36) * mm, "radius": 0.09 * mm});
            skCircle(sketch, "E33.2.8.20", {"center": v(1.14, -1.5) * mm, "radius": 0.09 * mm});
            skCircle(sketch, "E33.0.8.21", {"center": v(0.9, -1.59) * mm, "radius": 0.09 * mm});
            skCircle(sketch, "E33.2.8.21", {"center": v(1.14, -1.72) * mm, "radius": 0.09 * mm});
            skCircle(sketch, "E33.0.9.11", {"center": v(1.36, 0.68) * mm, "radius": 0.09 * mm});
            skCircle(sketch, "E33.2.9.11", {"center": v(1.6, 0.55) * mm, "radius": 0.09 * mm});
            skCircle(sketch, "E33.0.9.12", {"center": v(1.36, 0.46) * mm, "radius": 0.09 * mm});
            skCircle(sketch, "E33.2.9.12", {"center": v(1.6, 0.33) * mm, "radius": 0.09 * mm});
            skCircle(sketch, "E33.0.9.13", {"center": v(1.36, 0.23) * mm, "radius": 0.09 * mm});
            skCircle(sketch, "E33.2.9.13", {"center": v(1.6, 0.1) * mm, "radius": 0.09 * mm});
            skCircle(sketch, "E33.0.9.14", {"center": v(1.36, 0) * mm, "radius": 0.09 * mm});
            skCircle(sketch, "E33.2.9.14", {"center": v(1.6, -0.13) * mm, "radius": 0.09 * mm});
            skCircle(sketch, "E33.0.9.15", {"center": v(1.36, -0.22) * mm, "radius": 0.09 * mm});
            skCircle(sketch, "E33.2.9.15", {"center": v(1.6, -0.36) * mm, "radius": 0.09 * mm});
            skCircle(sketch, "E33.0.9.16", {"center": v(1.36, -0.45) * mm, "radius": 0.09 * mm});
            skCircle(sketch, "E33.2.9.16", {"center": v(1.6, -0.58) * mm, "radius": 0.09 * mm});
            skCircle(sketch, "E33.0.9.17", {"center": v(1.36, -0.68) * mm, "radius": 0.09 * mm});
            skCircle(sketch, "E33.2.9.17", {"center": v(1.6, -0.8) * mm, "radius": 0.09 * mm});
            skCircle(sketch, "E33.0.9.18", {"center": v(1.36, -0.9) * mm, "radius": 0.09 * mm});
            skCircle(sketch, "E33.2.9.18", {"center": v(1.6, -1.04) * mm, "radius": 0.09 * mm});
            skCircle(sketch, "E33.0.9.19", {"center": v(1.36, -1.13) * mm, "radius": 0.09 * mm});
            skCircle(sketch, "E33.2.9.19", {"center": v(1.6, -1.26) * mm, "radius": 0.09 * mm});
            skCircle(sketch, "E33.0.9.20", {"center": v(1.36, -1.36) * mm, "radius": 0.09 * mm});
            skCircle(sketch, "E33.2.9.20", {"center": v(1.6, -1.5) * mm, "radius": 0.09 * mm});
            skCircle(sketch, "E33.0.9.21", {"center": v(1.36, -1.59) * mm, "radius": 0.09 * mm});
            skCircle(sketch, "E33.2.9.21", {"center": v(1.6, -1.72) * mm, "radius": 0.09 * mm});
            skCircle(sketch, "E33.0.10.11", {"center": v(1.82, 0.68) * mm, "radius": 0.09 * mm});
            skCircle(sketch, "E33.2.10.11", {"center": v(2.04, 0.55) * mm, "radius": 0.09 * mm});
            skCircle(sketch, "E33.0.10.12", {"center": v(1.82, 0.46) * mm, "radius": 0.09 * mm});
            skCircle(sketch, "E33.2.10.12", {"center": v(2.04, 0.33) * mm, "radius": 0.09 * mm});
            skCircle(sketch, "E33.0.10.13", {"center": v(1.82, 0.23) * mm, "radius": 0.09 * mm});
            skCircle(sketch, "E33.2.10.13", {"center": v(2.04, 0.1) * mm, "radius": 0.09 * mm});
            skCircle(sketch, "E33.0.10.14", {"center": v(1.82, 0) * mm, "radius": 0.09 * mm});
            skCircle(sketch, "E33.2.10.14", {"center": v(2.04, -0.13) * mm, "radius": 0.09 * mm});
            skCircle(sketch, "E33.0.10.15", {"center": v(1.82, -0.22) * mm, "radius": 0.09 * mm});
            skCircle(sketch, "E33.2.10.15", {"center": v(2.04, -0.36) * mm, "radius": 0.09 * mm});
            skCircle(sketch, "E33.0.10.16", {"center": v(1.82, -0.45) * mm, "radius": 0.09 * mm});
            skCircle(sketch, "E33.2.10.16", {"center": v(2.04, -0.58) * mm, "radius": 0.09 * mm});
            skCircle(sketch, "E33.0.10.17", {"center": v(1.82, -0.68) * mm, "radius": 0.09 * mm});
            skCircle(sketch, "E33.2.10.17", {"center": v(2.04, -0.8) * mm, "radius": 0.09 * mm});
            skCircle(sketch, "E33.0.10.18", {"center": v(1.82, -0.9) * mm, "radius": 0.09 * mm});
            skCircle(sketch, "E33.2.10.18", {"center": v(2.04, -1.04) * mm, "radius": 0.09 * mm});
            skCircle(sketch, "E33.0.10.19", {"center": v(1.82, -1.13) * mm, "radius": 0.09 * mm});
            skCircle(sketch, "E33.2.10.19", {"center": v(2.04, -1.26) * mm, "radius": 0.09 * mm});
            skCircle(sketch, "E33.0.10.20", {"center": v(1.82, -1.36) * mm, "radius": 0.09 * mm});
            skCircle(sketch, "E33.0.10.21", {"center": v(1.82, -1.59) * mm, "radius": 0.09 * mm});
            skCircle(sketch, "E34.0.11.10", {"center": v(2.27, 0.91) * mm, "radius": 0.09 * mm});
            skCircle(sketch, "E34.0.11.11", {"center": v(2.27, 0.68) * mm, "radius": 0.09 * mm});
            skCircle(sketch, "E34.0.11.12", {"center": v(2.27, 0.46) * mm, "radius": 0.09 * mm});
            skCircle(sketch, "E34.0.11.13", {"center": v(2.27, 0.23) * mm, "radius": 0.09 * mm});
            skCircle(sketch, "E34.0.11.14", {"center": v(2.27, 0) * mm, "radius": 0.09 * mm});
            skCircle(sketch, "E34.0.11.15", {"center": v(2.27, -0.22) * mm, "radius": 0.09 * mm});
            skCircle(sketch, "E34.0.11.16", {"center": v(2.27, -0.45) * mm, "radius": 0.09 * mm});
            skCircle(sketch, "E34.0.11.17", {"center": v(2.27, -0.68) * mm, "radius": 0.09 * mm});
            skCircle(sketch, "E34.0.11.18", {"center": v(2.27, -0.9) * mm, "radius": 0.09 * mm});
            skCircle(sketch, "E35.0.3.22", {"center": v(-1.36, -1.81) * mm, "radius": 0.09 * mm});
            skCircle(sketch, "E35.2.3.22", {"center": v(-1.13, -1.94) * mm, "radius": 0.09 * mm});
            skCircle(sketch, "E35.0.3.23", {"center": v(-1.36, -2.04) * mm, "radius": 0.09 * mm});
            skCircle(sketch, "E35.2.3.23", {"center": v(-1.13, -2.17) * mm, "radius": 0.09 * mm});
            skCircle(sketch, "E35.0.4.22", {"center": v(-0.9, -1.81) * mm, "radius": 0.09 * mm});
            skCircle(sketch, "E35.2.4.22", {"center": v(-0.68, -1.94) * mm, "radius": 0.09 * mm});
            skCircle(sketch, "E35.0.4.23", {"center": v(-0.9, -2.04) * mm, "radius": 0.09 * mm});
            skCircle(sketch, "E35.2.4.23", {"center": v(-0.68, -2.17) * mm, "radius": 0.09 * mm});
            skCircle(sketch, "E35.0.4.24", {"center": v(-0.9, -2.27) * mm, "radius": 0.09 * mm});
            skCircle(sketch, "E35.0.5.22", {"center": v(-0.45, -1.81) * mm, "radius": 0.09 * mm});
            skCircle(sketch, "E35.2.5.22", {"center": v(-0.23, -1.94) * mm, "radius": 0.09 * mm});
            skCircle(sketch, "E35.0.5.23", {"center": v(-0.45, -2.04) * mm, "radius": 0.09 * mm});
            skCircle(sketch, "E35.2.5.23", {"center": v(-0.23, -2.17) * mm, "radius": 0.09 * mm});
            skCircle(sketch, "E35.0.5.24", {"center": v(-0.45, -2.27) * mm, "radius": 0.09 * mm});
            skCircle(sketch, "E35.2.5.24", {"center": v(-0.23, -2.4) * mm, "radius": 0.09 * mm});
            skCircle(sketch, "E35.0.6.22", {"center": v(0, -1.81) * mm, "radius": 0.09 * mm});
            skCircle(sketch, "E35.2.6.22", {"center": v(0.23, -1.94) * mm, "radius": 0.09 * mm});
            skCircle(sketch, "E35.0.6.23", {"center": v(0, -2.04) * mm, "radius": 0.09 * mm});
            skCircle(sketch, "E35.2.6.23", {"center": v(0.23, -2.17) * mm, "radius": 0.09 * mm});
            skCircle(sketch, "E35.0.6.24", {"center": v(0, -2.27) * mm, "radius": 0.09 * mm});
            skCircle(sketch, "E35.2.6.24", {"center": v(0.23, -2.4) * mm, "radius": 0.09 * mm});
            skCircle(sketch, "E35.0.7.22", {"center": v(0.45, -1.81) * mm, "radius": 0.09 * mm});
            skCircle(sketch, "E35.2.7.22", {"center": v(0.68, -1.94) * mm, "radius": 0.09 * mm});
            skCircle(sketch, "E35.0.7.23", {"center": v(0.45, -2.04) * mm, "radius": 0.09 * mm});
            skCircle(sketch, "E35.2.7.23", {"center": v(0.68, -2.17) * mm, "radius": 0.09 * mm});
            skCircle(sketch, "E35.0.7.24", {"center": v(0.45, -2.27) * mm, "radius": 0.09 * mm});
            skCircle(sketch, "E35.0.8.22", {"center": v(0.9, -1.81) * mm, "radius": 0.09 * mm});
            skCircle(sketch, "E35.2.8.22", {"center": v(1.14, -1.94) * mm, "radius": 0.09 * mm});
            skCircle(sketch, "E35.0.8.23", {"center": v(0.9, -2.04) * mm, "radius": 0.09 * mm});
            skCircle(sketch, "E35.2.8.23", {"center": v(1.14, -2.17) * mm, "radius": 0.09 * mm});
            skCircle(sketch, "E35.0.8.24", {"center": v(0.9, -2.27) * mm, "radius": 0.09 * mm});
            skCircle(sketch, "E35.0.9.22", {"center": v(1.36, -1.81) * mm, "radius": 0.09 * mm});
            skCircle(sketch, "E35.0.9.23", {"center": v(1.36, -2.04) * mm, "radius": 0.09 * mm});
            skCircle(sketch, "E36.0", {"center": v(0, 0) * mm, "radius": 2.5 * mm, "construction": true});
            skSolve(sketch);
        }
        {
            var Q0;
            Q0=qSketchRegion(id+"F3",true);
            extrude(context, id + "F4", {"entities" : qUnion([Q0]), "operationType" : NewBodyOperationType.REMOVE, "endBound" : BoundingType.THROUGH_ALL, "oppositeDirection" : true, "depth" : 25 * mm});
        }
        {
            var Q0;
            Q0=makeQuery(id+"F1.opExtrude","CAP_FACE",FACE,{"disambiguationData":[OSD([sQuery(id+"F0.wireOp",EDGE,"E4"),sQuery(id+"F0.wireOp",EDGE,"E5"),sQuery(id+"F0.wireOp",EDGE,"E6.1.0"),sQuery(id+"F0.wireOp",EDGE,"E6.1.1"),sQuery(id+"F0.wireOp",EDGE,"E6.2.0"),sQuery(id+"F0.wireOp",EDGE,"E6.2.1"),sQuery(id+"F0.wireOp",EDGE,"E6.3.0"),sQuery(id+"F0.wireOp",EDGE,"E6.3.1"),sQuery(id+"F0.wireOp",EDGE,"E6.4.0"),sQuery(id+"F0.wireOp",EDGE,"E6.4.1"),sQuery(id+"F0.wireOp",EDGE,"E6.5.0"),sQuery(id+"F0.wireOp",EDGE,"E6.5.1"),sQuery(id+"F0.wireOp",EDGE,"E6.6.0"),sQuery(id+"F0.wireOp",EDGE,"E6.6.1"),sQuery(id+"F0.wireOp",EDGE,"E6.7.0"),sQuery(id+"F0.wireOp",EDGE,"E6.7.1"),sQuery(id+"F0.wireOp",EDGE,"E6.8.0"),sQuery(id+"F0.wireOp",EDGE,"E6.8.1"),sQuery(id+"F0.wireOp",EDGE,"E6.9.0"),sQuery(id+"F0.wireOp",EDGE,"E6.9.1"),sQuery(id+"F0.wireOp",EDGE,"E9"),sQuery(id+"F0.wireOp",EDGE,"E10.1.0"),sQuery(id+"F0.wireOp",EDGE,"E10.2.0"),sQuery(id+"F0.wireOp",EDGE,"E10.3.0"),sQuery(id+"F0.wireOp",EDGE,"E10.4.0"),sQuery(id+"F0.wireOp",EDGE,"E10.5.0"),sQuery(id+"F0.wireOp",EDGE,"E10.6.0"),sQuery(id+"F0.wireOp",EDGE,"E10.7.0"),sQuery(id+"F0.wireOp",EDGE,"E10.8.0"),sQuery(id+"F0.wireOp",EDGE,"E10.9.0"),sQuery(id+"F0.wireOp",EDGE,"E11"),sQuery(id+"F0.wireOp",EDGE,"E12.trimOffspring"),sQuery(id+"F0.wireOp",EDGE,"E13.1.0"),sQuery(id+"F0.wireOp",EDGE,"E13.2.0"),sQuery(id+"F0.wireOp",EDGE,"E13.3.0"),sQuery(id+"F0.wireOp",EDGE,"E13.4.0"),sQuery(id+"F0.wireOp",EDGE,"E13.5.0"),sQuery(id+"F0.wireOp",EDGE,"E13.6.0"),sQuery(id+"F0.wireOp",EDGE,"E13.7.0"),sQuery(id+"F0.wireOp",EDGE,"E13.8.0"),sQuery(id+"F0.wireOp",EDGE,"E13.9.0"),sQuery(id+"F0.wireOp",EDGE,"E14.trimOffspring"),sQuery(id+"F0.wireOp",EDGE,"E16.trimOffspring"),sQuery(id+"F0.wireOp",EDGE,"E18.trimOffspring"),sQuery(id+"F0.wireOp",EDGE,"E20.trimOffspring"),sQuery(id+"F0.wireOp",EDGE,"E22.trimOffspring"),sQuery(id+"F0.wireOp",EDGE,"E24.trimOffspring"),sQuery(id+"F0.wireOp",EDGE,"E26.trimOffspring"),sQuery(id+"F0.wireOp",EDGE,"E28.trimOffspring"),sQuery(id+"F0.wireOp",EDGE,"E30.trimOffspring")])],"isStart":false});
            var sketch = newSketch(context, id + "F5", { "sketchPlane" : qUnion([Q0])});
            skCircle(sketch, "E37", {"center": v(0, 0) * mm, "radius": 2.75 * mm});
            skCircle(sketch, "E38", {"center": v(0, 0) * mm, "radius": 3.85 * mm});
            skSolve(sketch);
        }
        {
            var Q0;
            Q0=qSketchRegion(id+"F5",true);
            extrude(context, id + "F6", {"entities" : qUnion([Q0]), "operationType" : NewBodyOperationType.REMOVE, "oppositeDirection" : true, "depth" : 25 * mm});
        }
        {
            var Q0;
            Q0=makeQuery(id+"F1.opExtrude","CAP_FACE",FACE,{"disambiguationData":[OSD([sQuery(id+"F0.wireOp",EDGE,"E4"),sQuery(id+"F0.wireOp",EDGE,"E5"),sQuery(id+"F0.wireOp",EDGE,"E6.1.0"),sQuery(id+"F0.wireOp",EDGE,"E6.1.1"),sQuery(id+"F0.wireOp",EDGE,"E6.2.0"),sQuery(id+"F0.wireOp",EDGE,"E6.2.1"),sQuery(id+"F0.wireOp",EDGE,"E6.3.0"),sQuery(id+"F0.wireOp",EDGE,"E6.3.1"),sQuery(id+"F0.wireOp",EDGE,"E6.4.0"),sQuery(id+"F0.wireOp",EDGE,"E6.4.1"),sQuery(id+"F0.wireOp",EDGE,"E6.5.0"),sQuery(id+"F0.wireOp",EDGE,"E6.5.1"),sQuery(id+"F0.wireOp",EDGE,"E6.6.0"),sQuery(id+"F0.wireOp",EDGE,"E6.6.1"),sQuery(id+"F0.wireOp",EDGE,"E6.7.0"),sQuery(id+"F0.wireOp",EDGE,"E6.7.1"),sQuery(id+"F0.wireOp",EDGE,"E6.8.0"),sQuery(id+"F0.wireOp",EDGE,"E6.8.1"),sQuery(id+"F0.wireOp",EDGE,"E6.9.0"),sQuery(id+"F0.wireOp",EDGE,"E6.9.1"),sQuery(id+"F0.wireOp",EDGE,"E9"),sQuery(id+"F0.wireOp",EDGE,"E10.1.0"),sQuery(id+"F0.wireOp",EDGE,"E10.2.0"),sQuery(id+"F0.wireOp",EDGE,"E10.3.0"),sQuery(id+"F0.wireOp",EDGE,"E10.4.0"),sQuery(id+"F0.wireOp",EDGE,"E10.5.0"),sQuery(id+"F0.wireOp",EDGE,"E10.6.0"),sQuery(id+"F0.wireOp",EDGE,"E10.7.0"),sQuery(id+"F0.wireOp",EDGE,"E10.8.0"),sQuery(id+"F0.wireOp",EDGE,"E10.9.0"),sQuery(id+"F0.wireOp",EDGE,"E11"),sQuery(id+"F0.wireOp",EDGE,"E12.trimOffspring"),sQuery(id+"F0.wireOp",EDGE,"E13.1.0"),sQuery(id+"F0.wireOp",EDGE,"E13.2.0"),sQuery(id+"F0.wireOp",EDGE,"E13.3.0"),sQuery(id+"F0.wireOp",EDGE,"E13.4.0"),sQuery(id+"F0.wireOp",EDGE,"E13.5.0"),sQuery(id+"F0.wireOp",EDGE,"E13.6.0"),sQuery(id+"F0.wireOp",EDGE,"E13.7.0"),sQuery(id+"F0.wireOp",EDGE,"E13.8.0"),sQuery(id+"F0.wireOp",EDGE,"E13.9.0"),sQuery(id+"F0.wireOp",EDGE,"E14.trimOffspring"),sQuery(id+"F0.wireOp",EDGE,"E16.trimOffspring"),sQuery(id+"F0.wireOp",EDGE,"E18.trimOffspring"),sQuery(id+"F0.wireOp",EDGE,"E20.trimOffspring"),sQuery(id+"F0.wireOp",EDGE,"E22.trimOffspring"),sQuery(id+"F0.wireOp",EDGE,"E24.trimOffspring"),sQuery(id+"F0.wireOp",EDGE,"E26.trimOffspring"),sQuery(id+"F0.wireOp",EDGE,"E28.trimOffspring"),sQuery(id+"F0.wireOp",EDGE,"E30.trimOffspring")])],"isStart":false});
            var sketch = newSketch(context, id + "F7", { "sketchPlane" : qUnion([Q0])});
            skArc(sketch, "E39.0", {"start": v(-0.58, 2.69) * mm, "mid": v(-0.85, 2.62) * mm, "end": v(-1.1, 2.52) * mm});
            skCircle(sketch, "E40.0", {"center": v(0, 0) * mm, "radius": 2.62 * mm});
            skLineSegment(sketch, "E41", {"start": v(-1.1, 2.52) * mm, "end": v(-1.05, 2.4) * mm});
            skLineSegment(sketch, "E42", {"start": v(-0.58, 2.69) * mm, "end": v(-0.55, 2.57) * mm});
            skLineSegment(sketch, "E43", {"start": v(-0.33, 2.73) * mm, "end": v(-0.31, 2.6) * mm});
            skLineSegment(sketch, "E44", {"start": v(0.33, 2.73) * mm, "end": v(0.31, 2.6) * mm});
            skSolve(sketch);
        }
        {
            var Q0;
            {var subQ0=sQuery(id+"F7.wireOp",EDGE,"E43");Q0=makeQuery(id+"F7.imprint","IMPRINT",FACE,{"disambiguationData":[TD([[makeQuery(id+"F7.imprint","IMPRINT",EDGE,{"derivedFrom":subQ0}),1.0]])]});}
            extrude(context, id + "F8", {"entities" : qUnion([Q0]), "depth" : .762 * mm});
        }
        {
            var Q0;
            Q0=qCreatedBy(makeId("Front.planeOp"),FACE);
            var sketch = newSketch(context, id + "F9", { "sketchPlane" : qUnion([Q0])});
            skLineSegment(sketch, "E45", {"start": v(0, 3.9) * mm, "end": v(0, -4.13) * mm, "construction": true});
            skSolve(sketch);
        }
        {
            var Q0;
            Q0=qCreatedBy(makeId("Front.planeOp"),FACE);
            var sketch = newSketch(context, id + "F10", { "sketchPlane" : qUnion([Q0])});
            skLineSegment(sketch, "E46", {"start": v(0, 0.89) * mm, "end": v(0.33, 0.13) * mm});
            skLineSegment(sketch, "E47", {"start": v(0.33, 0.13) * mm, "end": v(-0.33, 0.13) * mm});
            skLineSegment(sketch, "E48", {"start": v(-0.33, 0.13) * mm, "end": v(0, 0.89) * mm});
            skPoint(sketch, "E49", {"position": v(0, 0.89) * mm});
            skPoint(sketch, "E50", {"position": v(-0.33, 0.13) * mm});
            skPoint(sketch, "E51", {"position": v(0.33, 0.13) * mm});
            skLineSegment(sketch, "E52", {"start": v(0.33, 0.13) * mm, "end": v(0.33, 0.89) * mm});
            skLineSegment(sketch, "E53", {"start": v(0.33, 0.89) * mm, "end": v(-0.33, 0.89) * mm});
            skLineSegment(sketch, "E54", {"start": v(-0.33, 0.89) * mm, "end": v(-0.33, 0.13) * mm});
            skSolve(sketch);
        }
        {
            var Q0;
            {var subQ0=sQuery(id+"F10.wireOp",EDGE,"E46");Q0=makeQuery(id+"F10.imprint","IMPRINT",FACE,{"disambiguationData":[TD([[makeQuery(id+"F10.imprint","IMPRINT",EDGE,{"derivedFrom":subQ0}),1.0]])]});}
            var Q1;
            {var subQ0=sQuery(id+"F10.wireOp",EDGE,"E48");Q1=makeQuery(id+"F10.imprint","IMPRINT",FACE,{"disambiguationData":[TD([[makeQuery(id+"F10.imprint","IMPRINT",EDGE,{"derivedFrom":subQ0}),1.0]])]});}
            extrude(context, id + "F11", {"entities" : qUnion([Q0, Q1]), "operationType" : NewBodyOperationType.REMOVE, "endBound" : BoundingType.THROUGH_ALL, "oppositeDirection" : true, "depth" : 25 * mm});
        }
        {
            var Q0;
            Q0=makeQuery(id+"F8.opExtrude","SWEPT_BODY",BODY,{"disambiguationData":[OSD([sQuery(id+"F5.wireOp",EDGE,"E37"),sQuery(id+"F7.wireOp",EDGE,"E40.0"),sQuery(id+"F7.wireOp",EDGE,"E43"),sQuery(id+"F7.wireOp",EDGE,"E44")])]});
            var Q1;
            Q1=sQuery(id+"F9.wireOp",EDGE,"E45");
            circularPattern(context, id + "F12", {"entities" : qUnion([Q0]), "axis" : qUnion([Q1]), "angle" : 360 * degree, "instanceCount" : 10, "equalSpace" : true});
        }
        {
            var Q0;
            Q0=makeQuery(id+"F6.boolean.opBoolean","INTERSECT",EDGE,{"disambiguationData":[OD(5.0)],"derivedFrom":[makeQuery(id+"F1.opExtrude","CAP_FACE",FACE,{"disambiguationData":[OSD([sQuery(id+"F0.wireOp",EDGE,"E4"),sQuery(id+"F0.wireOp",EDGE,"E5"),sQuery(id+"F0.wireOp",EDGE,"E6.1.0"),sQuery(id+"F0.wireOp",EDGE,"E6.1.1"),sQuery(id+"F0.wireOp",EDGE,"E6.2.0"),sQuery(id+"F0.wireOp",EDGE,"E6.2.1"),sQuery(id+"F0.wireOp",EDGE,"E6.3.0"),sQuery(id+"F0.wireOp",EDGE,"E6.3.1"),sQuery(id+"F0.wireOp",EDGE,"E6.4.0"),sQuery(id+"F0.wireOp",EDGE,"E6.4.1"),sQuery(id+"F0.wireOp",EDGE,"E6.5.0"),sQuery(id+"F0.wireOp",EDGE,"E6.5.1"),sQuery(id+"F0.wireOp",EDGE,"E6.6.0"),sQuery(id+"F0.wireOp",EDGE,"E6.6.1"),sQuery(id+"F0.wireOp",EDGE,"E6.7.0"),sQuery(id+"F0.wireOp",EDGE,"E6.7.1"),sQuery(id+"F0.wireOp",EDGE,"E6.8.0"),sQuery(id+"F0.wireOp",EDGE,"E6.8.1"),sQuery(id+"F0.wireOp",EDGE,"E6.9.0"),sQuery(id+"F0.wireOp",EDGE,"E6.9.1"),sQuery(id+"F0.wireOp",EDGE,"E9"),sQuery(id+"F0.wireOp",EDGE,"E10.1.0"),sQuery(id+"F0.wireOp",EDGE,"E10.2.0"),sQuery(id+"F0.wireOp",EDGE,"E10.3.0"),sQuery(id+"F0.wireOp",EDGE,"E10.4.0"),sQuery(id+"F0.wireOp",EDGE,"E10.5.0"),sQuery(id+"F0.wireOp",EDGE,"E10.6.0"),sQuery(id+"F0.wireOp",EDGE,"E10.7.0"),sQuery(id+"F0.wireOp",EDGE,"E10.8.0"),sQuery(id+"F0.wireOp",EDGE,"E10.9.0"),sQuery(id+"F0.wireOp",EDGE,"E11"),sQuery(id+"F0.wireOp",EDGE,"E12.trimOffspring"),sQuery(id+"F0.wireOp",EDGE,"E13.1.0"),sQuery(id+"F0.wireOp",EDGE,"E13.2.0"),sQuery(id+"F0.wireOp",EDGE,"E13.3.0"),sQuery(id+"F0.wireOp",EDGE,"E13.4.0"),sQuery(id+"F0.wireOp",EDGE,"E13.5.0"),sQuery(id+"F0.wireOp",EDGE,"E13.6.0"),sQuery(id+"F0.wireOp",EDGE,"E13.7.0"),sQuery(id+"F0.wireOp",EDGE,"E13.8.0"),sQuery(id+"F0.wireOp",EDGE,"E13.9.0"),sQuery(id+"F0.wireOp",EDGE,"E14.trimOffspring"),sQuery(id+"F0.wireOp",EDGE,"E16.trimOffspring"),sQuery(id+"F0.wireOp",EDGE,"E18.trimOffspring"),sQuery(id+"F0.wireOp",EDGE,"E20.trimOffspring"),sQuery(id+"F0.wireOp",EDGE,"E22.trimOffspring"),sQuery(id+"F0.wireOp",EDGE,"E24.trimOffspring"),sQuery(id+"F0.wireOp",EDGE,"E26.trimOffspring"),sQuery(id+"F0.wireOp",EDGE,"E28.trimOffspring"),sQuery(id+"F0.wireOp",EDGE,"E30.trimOffspring")])],"isStart":true}),makeQuery(id+"F6.opExtrude","SWEPT_FACE",FACE,{"disambiguationData":[OSD([sQuery(id+"F5.wireOp",EDGE,"E37")])]})]});
            var Q1;
            Q1=makeQuery(id+"F6.boolean.opBoolean","INTERSECT",EDGE,{"disambiguationData":[OD(6.0)],"derivedFrom":[makeQuery(id+"F1.opExtrude","CAP_FACE",FACE,{"disambiguationData":[OSD([sQuery(id+"F0.wireOp",EDGE,"E4"),sQuery(id+"F0.wireOp",EDGE,"E5"),sQuery(id+"F0.wireOp",EDGE,"E6.1.0"),sQuery(id+"F0.wireOp",EDGE,"E6.1.1"),sQuery(id+"F0.wireOp",EDGE,"E6.2.0"),sQuery(id+"F0.wireOp",EDGE,"E6.2.1"),sQuery(id+"F0.wireOp",EDGE,"E6.3.0"),sQuery(id+"F0.wireOp",EDGE,"E6.3.1"),sQuery(id+"F0.wireOp",EDGE,"E6.4.0"),sQuery(id+"F0.wireOp",EDGE,"E6.4.1"),sQuery(id+"F0.wireOp",EDGE,"E6.5.0"),sQuery(id+"F0.wireOp",EDGE,"E6.5.1"),sQuery(id+"F0.wireOp",EDGE,"E6.6.0"),sQuery(id+"F0.wireOp",EDGE,"E6.6.1"),sQuery(id+"F0.wireOp",EDGE,"E6.7.0"),sQuery(id+"F0.wireOp",EDGE,"E6.7.1"),sQuery(id+"F0.wireOp",EDGE,"E6.8.0"),sQuery(id+"F0.wireOp",EDGE,"E6.8.1"),sQuery(id+"F0.wireOp",EDGE,"E6.9.0"),sQuery(id+"F0.wireOp",EDGE,"E6.9.1"),sQuery(id+"F0.wireOp",EDGE,"E9"),sQuery(id+"F0.wireOp",EDGE,"E10.1.0"),sQuery(id+"F0.wireOp",EDGE,"E10.2.0"),sQuery(id+"F0.wireOp",EDGE,"E10.3.0"),sQuery(id+"F0.wireOp",EDGE,"E10.4.0"),sQuery(id+"F0.wireOp",EDGE,"E10.5.0"),sQuery(id+"F0.wireOp",EDGE,"E10.6.0"),sQuery(id+"F0.wireOp",EDGE,"E10.7.0"),sQuery(id+"F0.wireOp",EDGE,"E10.8.0"),sQuery(id+"F0.wireOp",EDGE,"E10.9.0"),sQuery(id+"F0.wireOp",EDGE,"E11"),sQuery(id+"F0.wireOp",EDGE,"E12.trimOffspring"),sQuery(id+"F0.wireOp",EDGE,"E13.1.0"),sQuery(id+"F0.wireOp",EDGE,"E13.2.0"),sQuery(id+"F0.wireOp",EDGE,"E13.3.0"),sQuery(id+"F0.wireOp",EDGE,"E13.4.0"),sQuery(id+"F0.wireOp",EDGE,"E13.5.0"),sQuery(id+"F0.wireOp",EDGE,"E13.6.0"),sQuery(id+"F0.wireOp",EDGE,"E13.7.0"),sQuery(id+"F0.wireOp",EDGE,"E13.8.0"),sQuery(id+"F0.wireOp",EDGE,"E13.9.0"),sQuery(id+"F0.wireOp",EDGE,"E14.trimOffspring"),sQuery(id+"F0.wireOp",EDGE,"E16.trimOffspring"),sQuery(id+"F0.wireOp",EDGE,"E18.trimOffspring"),sQuery(id+"F0.wireOp",EDGE,"E20.trimOffspring"),sQuery(id+"F0.wireOp",EDGE,"E22.trimOffspring"),sQuery(id+"F0.wireOp",EDGE,"E24.trimOffspring"),sQuery(id+"F0.wireOp",EDGE,"E26.trimOffspring"),sQuery(id+"F0.wireOp",EDGE,"E28.trimOffspring"),sQuery(id+"F0.wireOp",EDGE,"E30.trimOffspring")])],"isStart":true}),makeQuery(id+"F6.opExtrude","SWEPT_FACE",FACE,{"disambiguationData":[OSD([sQuery(id+"F5.wireOp",EDGE,"E37")])]})]});
            var Q2;
            Q2=makeQuery(id+"F6.boolean.opBoolean","INTERSECT",EDGE,{"disambiguationData":[OD(7.0)],"derivedFrom":[makeQuery(id+"F1.opExtrude","CAP_FACE",FACE,{"disambiguationData":[OSD([sQuery(id+"F0.wireOp",EDGE,"E4"),sQuery(id+"F0.wireOp",EDGE,"E5"),sQuery(id+"F0.wireOp",EDGE,"E6.1.0"),sQuery(id+"F0.wireOp",EDGE,"E6.1.1"),sQuery(id+"F0.wireOp",EDGE,"E6.2.0"),sQuery(id+"F0.wireOp",EDGE,"E6.2.1"),sQuery(id+"F0.wireOp",EDGE,"E6.3.0"),sQuery(id+"F0.wireOp",EDGE,"E6.3.1"),sQuery(id+"F0.wireOp",EDGE,"E6.4.0"),sQuery(id+"F0.wireOp",EDGE,"E6.4.1"),sQuery(id+"F0.wireOp",EDGE,"E6.5.0"),sQuery(id+"F0.wireOp",EDGE,"E6.5.1"),sQuery(id+"F0.wireOp",EDGE,"E6.6.0"),sQuery(id+"F0.wireOp",EDGE,"E6.6.1"),sQuery(id+"F0.wireOp",EDGE,"E6.7.0"),sQuery(id+"F0.wireOp",EDGE,"E6.7.1"),sQuery(id+"F0.wireOp",EDGE,"E6.8.0"),sQuery(id+"F0.wireOp",EDGE,"E6.8.1"),sQuery(id+"F0.wireOp",EDGE,"E6.9.0"),sQuery(id+"F0.wireOp",EDGE,"E6.9.1"),sQuery(id+"F0.wireOp",EDGE,"E9"),sQuery(id+"F0.wireOp",EDGE,"E10.1.0"),sQuery(id+"F0.wireOp",EDGE,"E10.2.0"),sQuery(id+"F0.wireOp",EDGE,"E10.3.0"),sQuery(id+"F0.wireOp",EDGE,"E10.4.0"),sQuery(id+"F0.wireOp",EDGE,"E10.5.0"),sQuery(id+"F0.wireOp",EDGE,"E10.6.0"),sQuery(id+"F0.wireOp",EDGE,"E10.7.0"),sQuery(id+"F0.wireOp",EDGE,"E10.8.0"),sQuery(id+"F0.wireOp",EDGE,"E10.9.0"),sQuery(id+"F0.wireOp",EDGE,"E11"),sQuery(id+"F0.wireOp",EDGE,"E12.trimOffspring"),sQuery(id+"F0.wireOp",EDGE,"E13.1.0"),sQuery(id+"F0.wireOp",EDGE,"E13.2.0"),sQuery(id+"F0.wireOp",EDGE,"E13.3.0"),sQuery(id+"F0.wireOp",EDGE,"E13.4.0"),sQuery(id+"F0.wireOp",EDGE,"E13.5.0"),sQuery(id+"F0.wireOp",EDGE,"E13.6.0"),sQuery(id+"F0.wireOp",EDGE,"E13.7.0"),sQuery(id+"F0.wireOp",EDGE,"E13.8.0"),sQuery(id+"F0.wireOp",EDGE,"E13.9.0"),sQuery(id+"F0.wireOp",EDGE,"E14.trimOffspring"),sQuery(id+"F0.wireOp",EDGE,"E16.trimOffspring"),sQuery(id+"F0.wireOp",EDGE,"E18.trimOffspring"),sQuery(id+"F0.wireOp",EDGE,"E20.trimOffspring"),sQuery(id+"F0.wireOp",EDGE,"E22.trimOffspring"),sQuery(id+"F0.wireOp",EDGE,"E24.trimOffspring"),sQuery(id+"F0.wireOp",EDGE,"E26.trimOffspring"),sQuery(id+"F0.wireOp",EDGE,"E28.trimOffspring"),sQuery(id+"F0.wireOp",EDGE,"E30.trimOffspring")])],"isStart":true}),makeQuery(id+"F6.opExtrude","SWEPT_FACE",FACE,{"disambiguationData":[OSD([sQuery(id+"F5.wireOp",EDGE,"E37")])]})]});
            var Q3;
            Q3=makeQuery(id+"F6.boolean.opBoolean","INTERSECT",EDGE,{"disambiguationData":[OD(8.0)],"derivedFrom":[makeQuery(id+"F1.opExtrude","CAP_FACE",FACE,{"disambiguationData":[OSD([sQuery(id+"F0.wireOp",EDGE,"E4"),sQuery(id+"F0.wireOp",EDGE,"E5"),sQuery(id+"F0.wireOp",EDGE,"E6.1.0"),sQuery(id+"F0.wireOp",EDGE,"E6.1.1"),sQuery(id+"F0.wireOp",EDGE,"E6.2.0"),sQuery(id+"F0.wireOp",EDGE,"E6.2.1"),sQuery(id+"F0.wireOp",EDGE,"E6.3.0"),sQuery(id+"F0.wireOp",EDGE,"E6.3.1"),sQuery(id+"F0.wireOp",EDGE,"E6.4.0"),sQuery(id+"F0.wireOp",EDGE,"E6.4.1"),sQuery(id+"F0.wireOp",EDGE,"E6.5.0"),sQuery(id+"F0.wireOp",EDGE,"E6.5.1"),sQuery(id+"F0.wireOp",EDGE,"E6.6.0"),sQuery(id+"F0.wireOp",EDGE,"E6.6.1"),sQuery(id+"F0.wireOp",EDGE,"E6.7.0"),sQuery(id+"F0.wireOp",EDGE,"E6.7.1"),sQuery(id+"F0.wireOp",EDGE,"E6.8.0"),sQuery(id+"F0.wireOp",EDGE,"E6.8.1"),sQuery(id+"F0.wireOp",EDGE,"E6.9.0"),sQuery(id+"F0.wireOp",EDGE,"E6.9.1"),sQuery(id+"F0.wireOp",EDGE,"E9"),sQuery(id+"F0.wireOp",EDGE,"E10.1.0"),sQuery(id+"F0.wireOp",EDGE,"E10.2.0"),sQuery(id+"F0.wireOp",EDGE,"E10.3.0"),sQuery(id+"F0.wireOp",EDGE,"E10.4.0"),sQuery(id+"F0.wireOp",EDGE,"E10.5.0"),sQuery(id+"F0.wireOp",EDGE,"E10.6.0"),sQuery(id+"F0.wireOp",EDGE,"E10.7.0"),sQuery(id+"F0.wireOp",EDGE,"E10.8.0"),sQuery(id+"F0.wireOp",EDGE,"E10.9.0"),sQuery(id+"F0.wireOp",EDGE,"E11"),sQuery(id+"F0.wireOp",EDGE,"E12.trimOffspring"),sQuery(id+"F0.wireOp",EDGE,"E13.1.0"),sQuery(id+"F0.wireOp",EDGE,"E13.2.0"),sQuery(id+"F0.wireOp",EDGE,"E13.3.0"),sQuery(id+"F0.wireOp",EDGE,"E13.4.0"),sQuery(id+"F0.wireOp",EDGE,"E13.5.0"),sQuery(id+"F0.wireOp",EDGE,"E13.6.0"),sQuery(id+"F0.wireOp",EDGE,"E13.7.0"),sQuery(id+"F0.wireOp",EDGE,"E13.8.0"),sQuery(id+"F0.wireOp",EDGE,"E13.9.0"),sQuery(id+"F0.wireOp",EDGE,"E14.trimOffspring"),sQuery(id+"F0.wireOp",EDGE,"E16.trimOffspring"),sQuery(id+"F0.wireOp",EDGE,"E18.trimOffspring"),sQuery(id+"F0.wireOp",EDGE,"E20.trimOffspring"),sQuery(id+"F0.wireOp",EDGE,"E22.trimOffspring"),sQuery(id+"F0.wireOp",EDGE,"E24.trimOffspring"),sQuery(id+"F0.wireOp",EDGE,"E26.trimOffspring"),sQuery(id+"F0.wireOp",EDGE,"E28.trimOffspring"),sQuery(id+"F0.wireOp",EDGE,"E30.trimOffspring")])],"isStart":true}),makeQuery(id+"F6.opExtrude","SWEPT_FACE",FACE,{"disambiguationData":[OSD([sQuery(id+"F5.wireOp",EDGE,"E37")])]})]});
            var Q4;
            Q4=makeQuery(id+"F6.boolean.opBoolean","INTERSECT",EDGE,{"disambiguationData":[OD(9.0)],"derivedFrom":[makeQuery(id+"F1.opExtrude","CAP_FACE",FACE,{"disambiguationData":[OSD([sQuery(id+"F0.wireOp",EDGE,"E4"),sQuery(id+"F0.wireOp",EDGE,"E5"),sQuery(id+"F0.wireOp",EDGE,"E6.1.0"),sQuery(id+"F0.wireOp",EDGE,"E6.1.1"),sQuery(id+"F0.wireOp",EDGE,"E6.2.0"),sQuery(id+"F0.wireOp",EDGE,"E6.2.1"),sQuery(id+"F0.wireOp",EDGE,"E6.3.0"),sQuery(id+"F0.wireOp",EDGE,"E6.3.1"),sQuery(id+"F0.wireOp",EDGE,"E6.4.0"),sQuery(id+"F0.wireOp",EDGE,"E6.4.1"),sQuery(id+"F0.wireOp",EDGE,"E6.5.0"),sQuery(id+"F0.wireOp",EDGE,"E6.5.1"),sQuery(id+"F0.wireOp",EDGE,"E6.6.0"),sQuery(id+"F0.wireOp",EDGE,"E6.6.1"),sQuery(id+"F0.wireOp",EDGE,"E6.7.0"),sQuery(id+"F0.wireOp",EDGE,"E6.7.1"),sQuery(id+"F0.wireOp",EDGE,"E6.8.0"),sQuery(id+"F0.wireOp",EDGE,"E6.8.1"),sQuery(id+"F0.wireOp",EDGE,"E6.9.0"),sQuery(id+"F0.wireOp",EDGE,"E6.9.1"),sQuery(id+"F0.wireOp",EDGE,"E9"),sQuery(id+"F0.wireOp",EDGE,"E10.1.0"),sQuery(id+"F0.wireOp",EDGE,"E10.2.0"),sQuery(id+"F0.wireOp",EDGE,"E10.3.0"),sQuery(id+"F0.wireOp",EDGE,"E10.4.0"),sQuery(id+"F0.wireOp",EDGE,"E10.5.0"),sQuery(id+"F0.wireOp",EDGE,"E10.6.0"),sQuery(id+"F0.wireOp",EDGE,"E10.7.0"),sQuery(id+"F0.wireOp",EDGE,"E10.8.0"),sQuery(id+"F0.wireOp",EDGE,"E10.9.0"),sQuery(id+"F0.wireOp",EDGE,"E11"),sQuery(id+"F0.wireOp",EDGE,"E12.trimOffspring"),sQuery(id+"F0.wireOp",EDGE,"E13.1.0"),sQuery(id+"F0.wireOp",EDGE,"E13.2.0"),sQuery(id+"F0.wireOp",EDGE,"E13.3.0"),sQuery(id+"F0.wireOp",EDGE,"E13.4.0"),sQuery(id+"F0.wireOp",EDGE,"E13.5.0"),sQuery(id+"F0.wireOp",EDGE,"E13.6.0"),sQuery(id+"F0.wireOp",EDGE,"E13.7.0"),sQuery(id+"F0.wireOp",EDGE,"E13.8.0"),sQuery(id+"F0.wireOp",EDGE,"E13.9.0"),sQuery(id+"F0.wireOp",EDGE,"E14.trimOffspring"),sQuery(id+"F0.wireOp",EDGE,"E16.trimOffspring"),sQuery(id+"F0.wireOp",EDGE,"E18.trimOffspring"),sQuery(id+"F0.wireOp",EDGE,"E20.trimOffspring"),sQuery(id+"F0.wireOp",EDGE,"E22.trimOffspring"),sQuery(id+"F0.wireOp",EDGE,"E24.trimOffspring"),sQuery(id+"F0.wireOp",EDGE,"E26.trimOffspring"),sQuery(id+"F0.wireOp",EDGE,"E28.trimOffspring"),sQuery(id+"F0.wireOp",EDGE,"E30.trimOffspring")])],"isStart":true}),makeQuery(id+"F6.opExtrude","SWEPT_FACE",FACE,{"disambiguationData":[OSD([sQuery(id+"F5.wireOp",EDGE,"E37")])]})]});
            var Q5;
            Q5=makeQuery(id+"F6.boolean.opBoolean","INTERSECT",EDGE,{"disambiguationData":[OD(0.0)],"derivedFrom":[makeQuery(id+"F1.opExtrude","CAP_FACE",FACE,{"disambiguationData":[OSD([sQuery(id+"F0.wireOp",EDGE,"E4"),sQuery(id+"F0.wireOp",EDGE,"E5"),sQuery(id+"F0.wireOp",EDGE,"E6.1.0"),sQuery(id+"F0.wireOp",EDGE,"E6.1.1"),sQuery(id+"F0.wireOp",EDGE,"E6.2.0"),sQuery(id+"F0.wireOp",EDGE,"E6.2.1"),sQuery(id+"F0.wireOp",EDGE,"E6.3.0"),sQuery(id+"F0.wireOp",EDGE,"E6.3.1"),sQuery(id+"F0.wireOp",EDGE,"E6.4.0"),sQuery(id+"F0.wireOp",EDGE,"E6.4.1"),sQuery(id+"F0.wireOp",EDGE,"E6.5.0"),sQuery(id+"F0.wireOp",EDGE,"E6.5.1"),sQuery(id+"F0.wireOp",EDGE,"E6.6.0"),sQuery(id+"F0.wireOp",EDGE,"E6.6.1"),sQuery(id+"F0.wireOp",EDGE,"E6.7.0"),sQuery(id+"F0.wireOp",EDGE,"E6.7.1"),sQuery(id+"F0.wireOp",EDGE,"E6.8.0"),sQuery(id+"F0.wireOp",EDGE,"E6.8.1"),sQuery(id+"F0.wireOp",EDGE,"E6.9.0"),sQuery(id+"F0.wireOp",EDGE,"E6.9.1"),sQuery(id+"F0.wireOp",EDGE,"E9"),sQuery(id+"F0.wireOp",EDGE,"E10.1.0"),sQuery(id+"F0.wireOp",EDGE,"E10.2.0"),sQuery(id+"F0.wireOp",EDGE,"E10.3.0"),sQuery(id+"F0.wireOp",EDGE,"E10.4.0"),sQuery(id+"F0.wireOp",EDGE,"E10.5.0"),sQuery(id+"F0.wireOp",EDGE,"E10.6.0"),sQuery(id+"F0.wireOp",EDGE,"E10.7.0"),sQuery(id+"F0.wireOp",EDGE,"E10.8.0"),sQuery(id+"F0.wireOp",EDGE,"E10.9.0"),sQuery(id+"F0.wireOp",EDGE,"E11"),sQuery(id+"F0.wireOp",EDGE,"E12.trimOffspring"),sQuery(id+"F0.wireOp",EDGE,"E13.1.0"),sQuery(id+"F0.wireOp",EDGE,"E13.2.0"),sQuery(id+"F0.wireOp",EDGE,"E13.3.0"),sQuery(id+"F0.wireOp",EDGE,"E13.4.0"),sQuery(id+"F0.wireOp",EDGE,"E13.5.0"),sQuery(id+"F0.wireOp",EDGE,"E13.6.0"),sQuery(id+"F0.wireOp",EDGE,"E13.7.0"),sQuery(id+"F0.wireOp",EDGE,"E13.8.0"),sQuery(id+"F0.wireOp",EDGE,"E13.9.0"),sQuery(id+"F0.wireOp",EDGE,"E14.trimOffspring"),sQuery(id+"F0.wireOp",EDGE,"E16.trimOffspring"),sQuery(id+"F0.wireOp",EDGE,"E18.trimOffspring"),sQuery(id+"F0.wireOp",EDGE,"E20.trimOffspring"),sQuery(id+"F0.wireOp",EDGE,"E22.trimOffspring"),sQuery(id+"F0.wireOp",EDGE,"E24.trimOffspring"),sQuery(id+"F0.wireOp",EDGE,"E26.trimOffspring"),sQuery(id+"F0.wireOp",EDGE,"E28.trimOffspring"),sQuery(id+"F0.wireOp",EDGE,"E30.trimOffspring")])],"isStart":true}),makeQuery(id+"F6.opExtrude","SWEPT_FACE",FACE,{"disambiguationData":[OSD([sQuery(id+"F5.wireOp",EDGE,"E37")])]})]});
            var Q6;
            Q6=makeQuery(id+"F6.boolean.opBoolean","INTERSECT",EDGE,{"disambiguationData":[OD(1.0)],"derivedFrom":[makeQuery(id+"F1.opExtrude","CAP_FACE",FACE,{"disambiguationData":[OSD([sQuery(id+"F0.wireOp",EDGE,"E4"),sQuery(id+"F0.wireOp",EDGE,"E5"),sQuery(id+"F0.wireOp",EDGE,"E6.1.0"),sQuery(id+"F0.wireOp",EDGE,"E6.1.1"),sQuery(id+"F0.wireOp",EDGE,"E6.2.0"),sQuery(id+"F0.wireOp",EDGE,"E6.2.1"),sQuery(id+"F0.wireOp",EDGE,"E6.3.0"),sQuery(id+"F0.wireOp",EDGE,"E6.3.1"),sQuery(id+"F0.wireOp",EDGE,"E6.4.0"),sQuery(id+"F0.wireOp",EDGE,"E6.4.1"),sQuery(id+"F0.wireOp",EDGE,"E6.5.0"),sQuery(id+"F0.wireOp",EDGE,"E6.5.1"),sQuery(id+"F0.wireOp",EDGE,"E6.6.0"),sQuery(id+"F0.wireOp",EDGE,"E6.6.1"),sQuery(id+"F0.wireOp",EDGE,"E6.7.0"),sQuery(id+"F0.wireOp",EDGE,"E6.7.1"),sQuery(id+"F0.wireOp",EDGE,"E6.8.0"),sQuery(id+"F0.wireOp",EDGE,"E6.8.1"),sQuery(id+"F0.wireOp",EDGE,"E6.9.0"),sQuery(id+"F0.wireOp",EDGE,"E6.9.1"),sQuery(id+"F0.wireOp",EDGE,"E9"),sQuery(id+"F0.wireOp",EDGE,"E10.1.0"),sQuery(id+"F0.wireOp",EDGE,"E10.2.0"),sQuery(id+"F0.wireOp",EDGE,"E10.3.0"),sQuery(id+"F0.wireOp",EDGE,"E10.4.0"),sQuery(id+"F0.wireOp",EDGE,"E10.5.0"),sQuery(id+"F0.wireOp",EDGE,"E10.6.0"),sQuery(id+"F0.wireOp",EDGE,"E10.7.0"),sQuery(id+"F0.wireOp",EDGE,"E10.8.0"),sQuery(id+"F0.wireOp",EDGE,"E10.9.0"),sQuery(id+"F0.wireOp",EDGE,"E11"),sQuery(id+"F0.wireOp",EDGE,"E12.trimOffspring"),sQuery(id+"F0.wireOp",EDGE,"E13.1.0"),sQuery(id+"F0.wireOp",EDGE,"E13.2.0"),sQuery(id+"F0.wireOp",EDGE,"E13.3.0"),sQuery(id+"F0.wireOp",EDGE,"E13.4.0"),sQuery(id+"F0.wireOp",EDGE,"E13.5.0"),sQuery(id+"F0.wireOp",EDGE,"E13.6.0"),sQuery(id+"F0.wireOp",EDGE,"E13.7.0"),sQuery(id+"F0.wireOp",EDGE,"E13.8.0"),sQuery(id+"F0.wireOp",EDGE,"E13.9.0"),sQuery(id+"F0.wireOp",EDGE,"E14.trimOffspring"),sQuery(id+"F0.wireOp",EDGE,"E16.trimOffspring"),sQuery(id+"F0.wireOp",EDGE,"E18.trimOffspring"),sQuery(id+"F0.wireOp",EDGE,"E20.trimOffspring"),sQuery(id+"F0.wireOp",EDGE,"E22.trimOffspring"),sQuery(id+"F0.wireOp",EDGE,"E24.trimOffspring"),sQuery(id+"F0.wireOp",EDGE,"E26.trimOffspring"),sQuery(id+"F0.wireOp",EDGE,"E28.trimOffspring"),sQuery(id+"F0.wireOp",EDGE,"E30.trimOffspring")])],"isStart":true}),makeQuery(id+"F6.opExtrude","SWEPT_FACE",FACE,{"disambiguationData":[OSD([sQuery(id+"F5.wireOp",EDGE,"E37")])]})]});
            var Q7;
            Q7=makeQuery(id+"F6.boolean.opBoolean","INTERSECT",EDGE,{"disambiguationData":[OD(2.0)],"derivedFrom":[makeQuery(id+"F1.opExtrude","CAP_FACE",FACE,{"disambiguationData":[OSD([sQuery(id+"F0.wireOp",EDGE,"E4"),sQuery(id+"F0.wireOp",EDGE,"E5"),sQuery(id+"F0.wireOp",EDGE,"E6.1.0"),sQuery(id+"F0.wireOp",EDGE,"E6.1.1"),sQuery(id+"F0.wireOp",EDGE,"E6.2.0"),sQuery(id+"F0.wireOp",EDGE,"E6.2.1"),sQuery(id+"F0.wireOp",EDGE,"E6.3.0"),sQuery(id+"F0.wireOp",EDGE,"E6.3.1"),sQuery(id+"F0.wireOp",EDGE,"E6.4.0"),sQuery(id+"F0.wireOp",EDGE,"E6.4.1"),sQuery(id+"F0.wireOp",EDGE,"E6.5.0"),sQuery(id+"F0.wireOp",EDGE,"E6.5.1"),sQuery(id+"F0.wireOp",EDGE,"E6.6.0"),sQuery(id+"F0.wireOp",EDGE,"E6.6.1"),sQuery(id+"F0.wireOp",EDGE,"E6.7.0"),sQuery(id+"F0.wireOp",EDGE,"E6.7.1"),sQuery(id+"F0.wireOp",EDGE,"E6.8.0"),sQuery(id+"F0.wireOp",EDGE,"E6.8.1"),sQuery(id+"F0.wireOp",EDGE,"E6.9.0"),sQuery(id+"F0.wireOp",EDGE,"E6.9.1"),sQuery(id+"F0.wireOp",EDGE,"E9"),sQuery(id+"F0.wireOp",EDGE,"E10.1.0"),sQuery(id+"F0.wireOp",EDGE,"E10.2.0"),sQuery(id+"F0.wireOp",EDGE,"E10.3.0"),sQuery(id+"F0.wireOp",EDGE,"E10.4.0"),sQuery(id+"F0.wireOp",EDGE,"E10.5.0"),sQuery(id+"F0.wireOp",EDGE,"E10.6.0"),sQuery(id+"F0.wireOp",EDGE,"E10.7.0"),sQuery(id+"F0.wireOp",EDGE,"E10.8.0"),sQuery(id+"F0.wireOp",EDGE,"E10.9.0"),sQuery(id+"F0.wireOp",EDGE,"E11"),sQuery(id+"F0.wireOp",EDGE,"E12.trimOffspring"),sQuery(id+"F0.wireOp",EDGE,"E13.1.0"),sQuery(id+"F0.wireOp",EDGE,"E13.2.0"),sQuery(id+"F0.wireOp",EDGE,"E13.3.0"),sQuery(id+"F0.wireOp",EDGE,"E13.4.0"),sQuery(id+"F0.wireOp",EDGE,"E13.5.0"),sQuery(id+"F0.wireOp",EDGE,"E13.6.0"),sQuery(id+"F0.wireOp",EDGE,"E13.7.0"),sQuery(id+"F0.wireOp",EDGE,"E13.8.0"),sQuery(id+"F0.wireOp",EDGE,"E13.9.0"),sQuery(id+"F0.wireOp",EDGE,"E14.trimOffspring"),sQuery(id+"F0.wireOp",EDGE,"E16.trimOffspring"),sQuery(id+"F0.wireOp",EDGE,"E18.trimOffspring"),sQuery(id+"F0.wireOp",EDGE,"E20.trimOffspring"),sQuery(id+"F0.wireOp",EDGE,"E22.trimOffspring"),sQuery(id+"F0.wireOp",EDGE,"E24.trimOffspring"),sQuery(id+"F0.wireOp",EDGE,"E26.trimOffspring"),sQuery(id+"F0.wireOp",EDGE,"E28.trimOffspring"),sQuery(id+"F0.wireOp",EDGE,"E30.trimOffspring")])],"isStart":true}),makeQuery(id+"F6.opExtrude","SWEPT_FACE",FACE,{"disambiguationData":[OSD([sQuery(id+"F5.wireOp",EDGE,"E37")])]})]});
            var Q8;
            Q8=makeQuery(id+"F6.boolean.opBoolean","INTERSECT",EDGE,{"disambiguationData":[OD(3.0)],"derivedFrom":[makeQuery(id+"F1.opExtrude","CAP_FACE",FACE,{"disambiguationData":[OSD([sQuery(id+"F0.wireOp",EDGE,"E4"),sQuery(id+"F0.wireOp",EDGE,"E5"),sQuery(id+"F0.wireOp",EDGE,"E6.1.0"),sQuery(id+"F0.wireOp",EDGE,"E6.1.1"),sQuery(id+"F0.wireOp",EDGE,"E6.2.0"),sQuery(id+"F0.wireOp",EDGE,"E6.2.1"),sQuery(id+"F0.wireOp",EDGE,"E6.3.0"),sQuery(id+"F0.wireOp",EDGE,"E6.3.1"),sQuery(id+"F0.wireOp",EDGE,"E6.4.0"),sQuery(id+"F0.wireOp",EDGE,"E6.4.1"),sQuery(id+"F0.wireOp",EDGE,"E6.5.0"),sQuery(id+"F0.wireOp",EDGE,"E6.5.1"),sQuery(id+"F0.wireOp",EDGE,"E6.6.0"),sQuery(id+"F0.wireOp",EDGE,"E6.6.1"),sQuery(id+"F0.wireOp",EDGE,"E6.7.0"),sQuery(id+"F0.wireOp",EDGE,"E6.7.1"),sQuery(id+"F0.wireOp",EDGE,"E6.8.0"),sQuery(id+"F0.wireOp",EDGE,"E6.8.1"),sQuery(id+"F0.wireOp",EDGE,"E6.9.0"),sQuery(id+"F0.wireOp",EDGE,"E6.9.1"),sQuery(id+"F0.wireOp",EDGE,"E9"),sQuery(id+"F0.wireOp",EDGE,"E10.1.0"),sQuery(id+"F0.wireOp",EDGE,"E10.2.0"),sQuery(id+"F0.wireOp",EDGE,"E10.3.0"),sQuery(id+"F0.wireOp",EDGE,"E10.4.0"),sQuery(id+"F0.wireOp",EDGE,"E10.5.0"),sQuery(id+"F0.wireOp",EDGE,"E10.6.0"),sQuery(id+"F0.wireOp",EDGE,"E10.7.0"),sQuery(id+"F0.wireOp",EDGE,"E10.8.0"),sQuery(id+"F0.wireOp",EDGE,"E10.9.0"),sQuery(id+"F0.wireOp",EDGE,"E11"),sQuery(id+"F0.wireOp",EDGE,"E12.trimOffspring"),sQuery(id+"F0.wireOp",EDGE,"E13.1.0"),sQuery(id+"F0.wireOp",EDGE,"E13.2.0"),sQuery(id+"F0.wireOp",EDGE,"E13.3.0"),sQuery(id+"F0.wireOp",EDGE,"E13.4.0"),sQuery(id+"F0.wireOp",EDGE,"E13.5.0"),sQuery(id+"F0.wireOp",EDGE,"E13.6.0"),sQuery(id+"F0.wireOp",EDGE,"E13.7.0"),sQuery(id+"F0.wireOp",EDGE,"E13.8.0"),sQuery(id+"F0.wireOp",EDGE,"E13.9.0"),sQuery(id+"F0.wireOp",EDGE,"E14.trimOffspring"),sQuery(id+"F0.wireOp",EDGE,"E16.trimOffspring"),sQuery(id+"F0.wireOp",EDGE,"E18.trimOffspring"),sQuery(id+"F0.wireOp",EDGE,"E20.trimOffspring"),sQuery(id+"F0.wireOp",EDGE,"E22.trimOffspring"),sQuery(id+"F0.wireOp",EDGE,"E24.trimOffspring"),sQuery(id+"F0.wireOp",EDGE,"E26.trimOffspring"),sQuery(id+"F0.wireOp",EDGE,"E28.trimOffspring"),sQuery(id+"F0.wireOp",EDGE,"E30.trimOffspring")])],"isStart":true}),makeQuery(id+"F6.opExtrude","SWEPT_FACE",FACE,{"disambiguationData":[OSD([sQuery(id+"F5.wireOp",EDGE,"E37")])]})]});
            var Q9;
            Q9=makeQuery(id+"F6.boolean.opBoolean","INTERSECT",EDGE,{"disambiguationData":[OD(4.0)],"derivedFrom":[makeQuery(id+"F1.opExtrude","CAP_FACE",FACE,{"disambiguationData":[OSD([sQuery(id+"F0.wireOp",EDGE,"E4"),sQuery(id+"F0.wireOp",EDGE,"E5"),sQuery(id+"F0.wireOp",EDGE,"E6.1.0"),sQuery(id+"F0.wireOp",EDGE,"E6.1.1"),sQuery(id+"F0.wireOp",EDGE,"E6.2.0"),sQuery(id+"F0.wireOp",EDGE,"E6.2.1"),sQuery(id+"F0.wireOp",EDGE,"E6.3.0"),sQuery(id+"F0.wireOp",EDGE,"E6.3.1"),sQuery(id+"F0.wireOp",EDGE,"E6.4.0"),sQuery(id+"F0.wireOp",EDGE,"E6.4.1"),sQuery(id+"F0.wireOp",EDGE,"E6.5.0"),sQuery(id+"F0.wireOp",EDGE,"E6.5.1"),sQuery(id+"F0.wireOp",EDGE,"E6.6.0"),sQuery(id+"F0.wireOp",EDGE,"E6.6.1"),sQuery(id+"F0.wireOp",EDGE,"E6.7.0"),sQuery(id+"F0.wireOp",EDGE,"E6.7.1"),sQuery(id+"F0.wireOp",EDGE,"E6.8.0"),sQuery(id+"F0.wireOp",EDGE,"E6.8.1"),sQuery(id+"F0.wireOp",EDGE,"E6.9.0"),sQuery(id+"F0.wireOp",EDGE,"E6.9.1"),sQuery(id+"F0.wireOp",EDGE,"E9"),sQuery(id+"F0.wireOp",EDGE,"E10.1.0"),sQuery(id+"F0.wireOp",EDGE,"E10.2.0"),sQuery(id+"F0.wireOp",EDGE,"E10.3.0"),sQuery(id+"F0.wireOp",EDGE,"E10.4.0"),sQuery(id+"F0.wireOp",EDGE,"E10.5.0"),sQuery(id+"F0.wireOp",EDGE,"E10.6.0"),sQuery(id+"F0.wireOp",EDGE,"E10.7.0"),sQuery(id+"F0.wireOp",EDGE,"E10.8.0"),sQuery(id+"F0.wireOp",EDGE,"E10.9.0"),sQuery(id+"F0.wireOp",EDGE,"E11"),sQuery(id+"F0.wireOp",EDGE,"E12.trimOffspring"),sQuery(id+"F0.wireOp",EDGE,"E13.1.0"),sQuery(id+"F0.wireOp",EDGE,"E13.2.0"),sQuery(id+"F0.wireOp",EDGE,"E13.3.0"),sQuery(id+"F0.wireOp",EDGE,"E13.4.0"),sQuery(id+"F0.wireOp",EDGE,"E13.5.0"),sQuery(id+"F0.wireOp",EDGE,"E13.6.0"),sQuery(id+"F0.wireOp",EDGE,"E13.7.0"),sQuery(id+"F0.wireOp",EDGE,"E13.8.0"),sQuery(id+"F0.wireOp",EDGE,"E13.9.0"),sQuery(id+"F0.wireOp",EDGE,"E14.trimOffspring"),sQuery(id+"F0.wireOp",EDGE,"E16.trimOffspring"),sQuery(id+"F0.wireOp",EDGE,"E18.trimOffspring"),sQuery(id+"F0.wireOp",EDGE,"E20.trimOffspring"),sQuery(id+"F0.wireOp",EDGE,"E22.trimOffspring"),sQuery(id+"F0.wireOp",EDGE,"E24.trimOffspring"),sQuery(id+"F0.wireOp",EDGE,"E26.trimOffspring"),sQuery(id+"F0.wireOp",EDGE,"E28.trimOffspring"),sQuery(id+"F0.wireOp",EDGE,"E30.trimOffspring")])],"isStart":true}),makeQuery(id+"F6.opExtrude","SWEPT_FACE",FACE,{"disambiguationData":[OSD([sQuery(id+"F5.wireOp",EDGE,"E37")])]})]});
            fillet(context, id + "F13", {"entities" : qUnion([Q0, Q1, Q2, Q3, Q4, Q5, Q6, Q7, Q8, Q9]), "radius" : .1 * mm, "tangentPropagation" : true, "allowEdgeOverflow" : false});
        }
        {
            var Q0;
            Q0=makeQuery(id+"F12.opPattern","COPY",EDGE,{"derivedFrom":makeQuery(id+"F8.opExtrude","CAP_EDGE",EDGE,{"disambiguationData":[OSD([sQuery(id+"F7.wireOp",EDGE,"E40.0")])],"isStart":true}),"instanceName":"8"});
            var Q1;
            Q1=makeQuery(id+"F12.opPattern","COPY",EDGE,{"derivedFrom":makeQuery(id+"F8.opExtrude","CAP_EDGE",EDGE,{"disambiguationData":[OSD([sQuery(id+"F7.wireOp",EDGE,"E40.0")])],"isStart":true}),"instanceName":"4"});
            var Q2;
            Q2=makeQuery(id+"F12.opPattern","COPY",EDGE,{"derivedFrom":makeQuery(id+"F8.opExtrude","CAP_EDGE",EDGE,{"disambiguationData":[OSD([sQuery(id+"F7.wireOp",EDGE,"E40.0")])],"isStart":true}),"instanceName":"5"});
            var Q3;
            Q3=makeQuery(id+"F12.opPattern","COPY",EDGE,{"derivedFrom":makeQuery(id+"F8.opExtrude","CAP_EDGE",EDGE,{"disambiguationData":[OSD([sQuery(id+"F7.wireOp",EDGE,"E40.0")])],"isStart":true}),"instanceName":"6"});
            var Q4;
            Q4=makeQuery(id+"F12.opPattern","COPY",EDGE,{"derivedFrom":makeQuery(id+"F8.opExtrude","CAP_EDGE",EDGE,{"disambiguationData":[OSD([sQuery(id+"F7.wireOp",EDGE,"E40.0")])],"isStart":true}),"instanceName":"3"});
            var Q5;
            Q5=makeQuery(id+"F12.opPattern","COPY",EDGE,{"derivedFrom":makeQuery(id+"F8.opExtrude","CAP_EDGE",EDGE,{"disambiguationData":[OSD([sQuery(id+"F7.wireOp",EDGE,"E40.0")])],"isStart":true}),"instanceName":"7"});
            var Q6;
            Q6=makeQuery(id+"F12.opPattern","COPY",EDGE,{"derivedFrom":makeQuery(id+"F8.opExtrude","CAP_EDGE",EDGE,{"disambiguationData":[OSD([sQuery(id+"F7.wireOp",EDGE,"E40.0")])],"isStart":true}),"instanceName":"9"});
            var Q7;
            Q7=makeQuery(id+"F8.opExtrude","CAP_EDGE",EDGE,{"disambiguationData":[OSD([sQuery(id+"F7.wireOp",EDGE,"E40.0")])],"isStart":true});
            var Q8;
            Q8=makeQuery(id+"F12.opPattern","COPY",EDGE,{"derivedFrom":makeQuery(id+"F8.opExtrude","CAP_EDGE",EDGE,{"disambiguationData":[OSD([sQuery(id+"F7.wireOp",EDGE,"E40.0")])],"isStart":true}),"instanceName":"1"});
            var Q9;
            Q9=makeQuery(id+"F12.opPattern","COPY",EDGE,{"derivedFrom":makeQuery(id+"F8.opExtrude","CAP_EDGE",EDGE,{"disambiguationData":[OSD([sQuery(id+"F7.wireOp",EDGE,"E40.0")])],"isStart":true}),"instanceName":"2"});
            fillet(context, id + "F14", {"entities" : qUnion([Q0, Q1, Q2, Q3, Q4, Q5, Q6, Q7, Q8, Q9]), "radius" : .8 * mm, "tangentPropagation" : true, "allowEdgeOverflow" : false});
        }
    });
